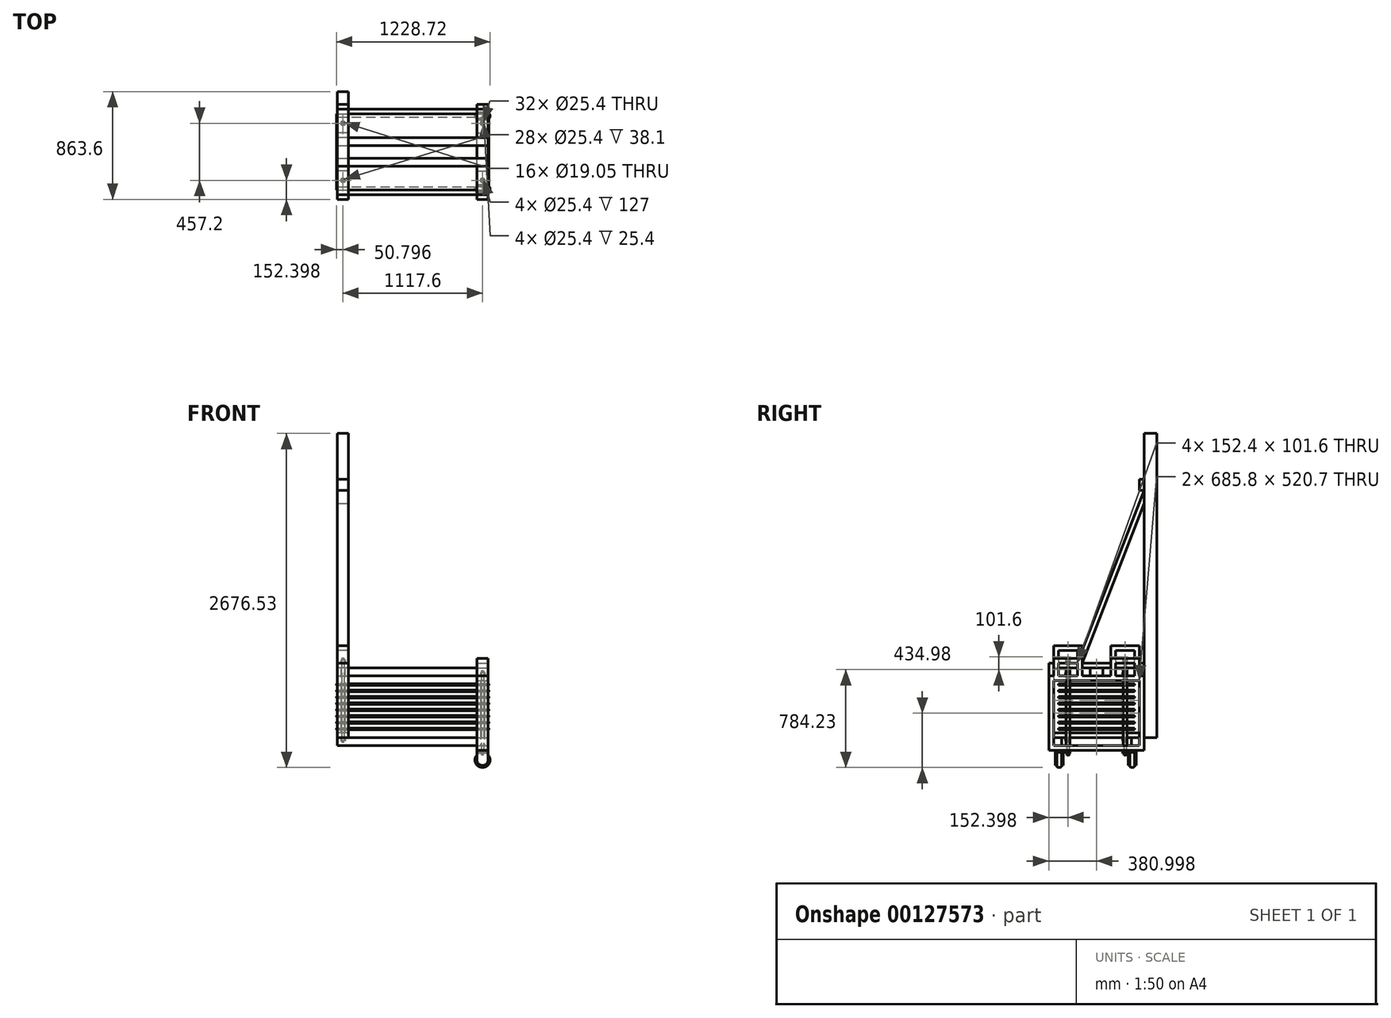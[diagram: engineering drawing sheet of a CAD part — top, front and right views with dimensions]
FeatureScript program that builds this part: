
annotation { "Feature Type Name" : "Feature", "Feature Type Description" : "" }
export const myFeature = defineFeature(function(context is Context, id is Id, definition is map)
    precondition{}
    {
        {
            var Q0;
            Q0=qCreatedBy(makeId("Top.planeOp"),FACE);
            var sketch = newSketch(context, id + "F0", { "sketchPlane" : qUnion([Q0])});
            skLineSegment(sketch, "E0.bottom", {"start": v(-608.46, 317.3) * mm, "end": v(610.74, 317.3) * mm});
            skLineSegment(sketch, "E0.top", {"start": v(-608.46, -292.3) * mm, "end": v(610.74, -292.3) * mm});
            skLineSegment(sketch, "E0.left", {"start": v(-608.46, 317.3) * mm, "end": v(-608.46, -292.3) * mm});
            skLineSegment(sketch, "E0.right", {"start": v(610.74, 317.3) * mm, "end": v(610.74, -292.3) * mm});
            skLineSegment(sketch, "E1", {"start": v(-608.46, 12.5) * mm, "end": v(-557.66, 12.5) * mm, "construction": true});
            skLineSegment(sketch, "E2", {"start": v(-557.66, 12.5) * mm, "end": v(559.94, 12.5) * mm, "construction": true});
            skPoint(sketch, "E2.endSnap0", {"position": v(610.74, 12.5) * mm});
            skLineSegment(sketch, "E3", {"start": v(559.94, 12.5) * mm, "end": v(610.74, 12.5) * mm, "construction": true});
            skLineSegment(sketch, "E4", {"start": v(-557.66, 12.5) * mm, "end": v(-557.66, 241.1) * mm, "construction": true});
            skLineSegment(sketch, "E5", {"start": v(-557.66, 241.1) * mm, "end": v(-557.66, 317.3) * mm, "construction": true});
            skLineSegment(sketch, "E6", {"start": v(-557.66, 12.5) * mm, "end": v(-557.66, -216.1) * mm, "construction": true});
            skLineSegment(sketch, "E7", {"start": v(-557.66, -216.1) * mm, "end": v(-557.66, -292.3) * mm, "construction": true});
            skLineSegment(sketch, "E8", {"start": v(559.94, 12.5) * mm, "end": v(559.94, 241.1) * mm, "construction": true});
            skLineSegment(sketch, "E9", {"start": v(559.94, 241.1) * mm, "end": v(559.94, 317.3) * mm, "construction": true});
            skLineSegment(sketch, "E10", {"start": v(559.94, 12.5) * mm, "end": v(559.94, -216.1) * mm, "construction": true});
            skLineSegment(sketch, "E11", {"start": v(559.94, -216.1) * mm, "end": v(559.94, -292.3) * mm, "construction": true});
            skCircle(sketch, "E12", {"center": v(-557.66, 241.1) * mm, "radius": 12.7 * mm});
            skCircle(sketch, "E13", {"center": v(-557.66, -216.1) * mm, "radius": 12.7 * mm});
            skCircle(sketch, "E14", {"center": v(559.94, 241.1) * mm, "radius": 12.7 * mm});
            skCircle(sketch, "E15", {"center": v(559.94, -216.1) * mm, "radius": 12.7 * mm});
            skSolve(sketch);
        }
        {
            var Q0;
            Q0 = qSketchRegion(id + "F0", true);
            extrude(context, id + "F1", {"entities" : qUnion([Q0]), "depth" : 12.7 * mm});
        }
        {
            var Q0;
            Q0=makeQuery(id+"F1.opExtrude","SWEPT_BODY",BODY,{"disambiguationData":[OSD([sQuery(id+"F0.wireOp",EDGE,"E0.bottom"),sQuery(id+"F0.wireOp",EDGE,"E0.top"),sQuery(id+"F0.wireOp",EDGE,"E0.left"),sQuery(id+"F0.wireOp",EDGE,"E0.right"),sQuery(id+"F0.wireOp",EDGE,"E12"),sQuery(id+"F0.wireOp",EDGE,"E13"),sQuery(id+"F0.wireOp",EDGE,"E14"),sQuery(id+"F0.wireOp",EDGE,"E15")])]});
            transform(context, id + "F2", {"entities" : qUnion([Q0]), "transformType" : TransformType.TRANSLATION_3D, "dx" : 0 * mm, "dy" : 0 * mm, "dz" : -50.8 * mm, "makeCopy" : true});
        }
        {
            var Q0;
            Q0=makeQuery(id+"F2.opPattern","COPY",BODY,{"derivedFrom":makeQuery(id+"F1.opExtrude","SWEPT_BODY",BODY,{"disambiguationData":[OSD([sQuery(id+"F0.wireOp",EDGE,"E0.bottom"),sQuery(id+"F0.wireOp",EDGE,"E0.top"),sQuery(id+"F0.wireOp",EDGE,"E0.left"),sQuery(id+"F0.wireOp",EDGE,"E0.right"),sQuery(id+"F0.wireOp",EDGE,"E12"),sQuery(id+"F0.wireOp",EDGE,"E13"),sQuery(id+"F0.wireOp",EDGE,"E14"),sQuery(id+"F0.wireOp",EDGE,"E15")])]}),"instanceName":"1"});
            transform(context, id + "F3", {"entities" : qUnion([Q0]), "transformType" : TransformType.TRANSLATION_3D, "dx" : 0 * mm, "dy" : 0 * mm, "dz" : -50.8 * mm, "makeCopy" : true});
        }
        {
            var Q0;
            Q0=makeQuery(id+"F3.opPattern","COPY",BODY,{"derivedFrom":makeQuery(id+"F2.opPattern","COPY",BODY,{"derivedFrom":makeQuery(id+"F1.opExtrude","SWEPT_BODY",BODY,{"disambiguationData":[OSD([sQuery(id+"F0.wireOp",EDGE,"E0.bottom"),sQuery(id+"F0.wireOp",EDGE,"E0.top"),sQuery(id+"F0.wireOp",EDGE,"E0.left"),sQuery(id+"F0.wireOp",EDGE,"E0.right"),sQuery(id+"F0.wireOp",EDGE,"E12"),sQuery(id+"F0.wireOp",EDGE,"E13"),sQuery(id+"F0.wireOp",EDGE,"E14"),sQuery(id+"F0.wireOp",EDGE,"E15")])]}),"instanceName":"1"}),"instanceName":"1"});
            transform(context, id + "F4", {"entities" : qUnion([Q0]), "transformType" : TransformType.TRANSLATION_3D, "dx" : 0 * mm, "dy" : 0 * mm, "dz" : -50.8 * mm, "makeCopy" : true});
        }
        {
            var Q0;
            Q0=makeQuery(id+"F4.opPattern","COPY",BODY,{"derivedFrom":makeQuery(id+"F3.opPattern","COPY",BODY,{"derivedFrom":makeQuery(id+"F2.opPattern","COPY",BODY,{"derivedFrom":makeQuery(id+"F1.opExtrude","SWEPT_BODY",BODY,{"disambiguationData":[OSD([sQuery(id+"F0.wireOp",EDGE,"E0.bottom"),sQuery(id+"F0.wireOp",EDGE,"E0.top"),sQuery(id+"F0.wireOp",EDGE,"E0.left"),sQuery(id+"F0.wireOp",EDGE,"E0.right"),sQuery(id+"F0.wireOp",EDGE,"E12"),sQuery(id+"F0.wireOp",EDGE,"E13"),sQuery(id+"F0.wireOp",EDGE,"E14"),sQuery(id+"F0.wireOp",EDGE,"E15")])]}),"instanceName":"1"}),"instanceName":"1"}),"instanceName":"1"});
            transform(context, id + "F5", {"entities" : qUnion([Q0]), "transformType" : TransformType.TRANSLATION_3D, "dx" : 0 * mm, "dy" : 0 * mm, "dz" : -50.8 * mm, "makeCopy" : true});
        }
        {
            var Q0;
            Q0=makeQuery(id+"F5.opPattern","COPY",BODY,{"derivedFrom":makeQuery(id+"F4.opPattern","COPY",BODY,{"derivedFrom":makeQuery(id+"F3.opPattern","COPY",BODY,{"derivedFrom":makeQuery(id+"F2.opPattern","COPY",BODY,{"derivedFrom":makeQuery(id+"F1.opExtrude","SWEPT_BODY",BODY,{"disambiguationData":[OSD([sQuery(id+"F0.wireOp",EDGE,"E0.bottom"),sQuery(id+"F0.wireOp",EDGE,"E0.top"),sQuery(id+"F0.wireOp",EDGE,"E0.left"),sQuery(id+"F0.wireOp",EDGE,"E0.right"),sQuery(id+"F0.wireOp",EDGE,"E12"),sQuery(id+"F0.wireOp",EDGE,"E13"),sQuery(id+"F0.wireOp",EDGE,"E14"),sQuery(id+"F0.wireOp",EDGE,"E15")])]}),"instanceName":"1"}),"instanceName":"1"}),"instanceName":"1"}),"instanceName":"1"});
            transform(context, id + "F6", {"entities" : qUnion([Q0]), "transformType" : TransformType.TRANSLATION_3D, "dx" : 0 * mm, "dy" : 0 * mm, "dz" : -50.8 * mm, "makeCopy" : true});
        }
        {
            var Q0;
            Q0=makeQuery(id+"F6.opPattern","COPY",BODY,{"derivedFrom":makeQuery(id+"F5.opPattern","COPY",BODY,{"derivedFrom":makeQuery(id+"F4.opPattern","COPY",BODY,{"derivedFrom":makeQuery(id+"F3.opPattern","COPY",BODY,{"derivedFrom":makeQuery(id+"F2.opPattern","COPY",BODY,{"derivedFrom":makeQuery(id+"F1.opExtrude","SWEPT_BODY",BODY,{"disambiguationData":[OSD([sQuery(id+"F0.wireOp",EDGE,"E0.bottom"),sQuery(id+"F0.wireOp",EDGE,"E0.top"),sQuery(id+"F0.wireOp",EDGE,"E0.left"),sQuery(id+"F0.wireOp",EDGE,"E0.right"),sQuery(id+"F0.wireOp",EDGE,"E12"),sQuery(id+"F0.wireOp",EDGE,"E13"),sQuery(id+"F0.wireOp",EDGE,"E14"),sQuery(id+"F0.wireOp",EDGE,"E15")])]}),"instanceName":"1"}),"instanceName":"1"}),"instanceName":"1"}),"instanceName":"1"}),"instanceName":"1"});
            transform(context, id + "F7", {"entities" : qUnion([Q0]), "transformType" : TransformType.TRANSLATION_3D, "dx" : 0 * mm, "dy" : 0 * mm, "dz" : -50.8 * mm, "makeCopy" : true});
        }
        {
            var Q0;
            Q0=makeQuery(id+"F7.opPattern","COPY",BODY,{"derivedFrom":makeQuery(id+"F6.opPattern","COPY",BODY,{"derivedFrom":makeQuery(id+"F5.opPattern","COPY",BODY,{"derivedFrom":makeQuery(id+"F4.opPattern","COPY",BODY,{"derivedFrom":makeQuery(id+"F3.opPattern","COPY",BODY,{"derivedFrom":makeQuery(id+"F2.opPattern","COPY",BODY,{"derivedFrom":makeQuery(id+"F1.opExtrude","SWEPT_BODY",BODY,{"disambiguationData":[OSD([sQuery(id+"F0.wireOp",EDGE,"E0.bottom"),sQuery(id+"F0.wireOp",EDGE,"E0.top"),sQuery(id+"F0.wireOp",EDGE,"E0.left"),sQuery(id+"F0.wireOp",EDGE,"E0.right"),sQuery(id+"F0.wireOp",EDGE,"E12"),sQuery(id+"F0.wireOp",EDGE,"E13"),sQuery(id+"F0.wireOp",EDGE,"E14"),sQuery(id+"F0.wireOp",EDGE,"E15")])]}),"instanceName":"1"}),"instanceName":"1"}),"instanceName":"1"}),"instanceName":"1"}),"instanceName":"1"}),"instanceName":"1"});
            transform(context, id + "F8", {"entities" : qUnion([Q0]), "transformType" : TransformType.TRANSLATION_3D, "dx" : 0 * mm, "dy" : 0 * mm, "dz" : -50.8 * mm, "makeCopy" : true});
        }
        {
            var Q0;
            Q0=makeQuery(id+"F1.opExtrude","CAP_FACE",FACE,{"disambiguationData":[OSD([sQuery(id+"F0.wireOp",EDGE,"E0.bottom"),sQuery(id+"F0.wireOp",EDGE,"E0.top"),sQuery(id+"F0.wireOp",EDGE,"E0.left"),sQuery(id+"F0.wireOp",EDGE,"E0.right"),sQuery(id+"F0.wireOp",EDGE,"E12"),sQuery(id+"F0.wireOp",EDGE,"E13"),sQuery(id+"F0.wireOp",EDGE,"E14"),sQuery(id+"F0.wireOp",EDGE,"E15")])],"isStart":false});
            var sketch = newSketch(context, id + "F9", { "sketchPlane" : qUnion([Q0])});
            skCircle(sketch, "E16", {"center": v(-557.66, 241.1) * mm, "radius": 15.88 * mm});
            skCircle(sketch, "E17", {"center": v(-557.66, -216.1) * mm, "radius": 15.88 * mm});
            skCircle(sketch, "E18", {"center": v(559.94, 241.1) * mm, "radius": 15.88 * mm});
            skCircle(sketch, "E19", {"center": v(559.94, -216.1) * mm, "radius": 15.88 * mm});
            skCircle(sketch, "E20", {"center": v(-557.66, 241.1) * mm, "radius": 12.7 * mm});
            skCircle(sketch, "E21", {"center": v(-557.66, -216.1) * mm, "radius": 12.7 * mm});
            skCircle(sketch, "E22", {"center": v(559.94, 241.1) * mm, "radius": 12.7 * mm});
            skCircle(sketch, "E23", {"center": v(559.94, -216.1) * mm, "radius": 12.7 * mm});
            skCircle(sketch, "E24", {"center": v(-557.66, 241.1) * mm, "radius": 9.53 * mm});
            skCircle(sketch, "E25", {"center": v(-557.66, -216.1) * mm, "radius": 9.53 * mm});
            skCircle(sketch, "E26", {"center": v(559.94, 241.1) * mm, "radius": 9.53 * mm});
            skCircle(sketch, "E27", {"center": v(559.94, -216.1) * mm, "radius": 9.53 * mm});
            skSolve(sketch);
        }
        {
            var Q0;
            Q0=makeQuery(id+"F9.imprint","IMPRINT",FACE,{"disambiguationData":[TD([[makeQuery(id+"F9.imprint","IMPRINT",EDGE,{"derivedFrom":sQuery(id+"F9.wireOp",EDGE,"E16")}),1.0]])]});
            var Q1;
            Q1=makeQuery(id+"F9.imprint","IMPRINT",FACE,{"disambiguationData":[TD([[makeQuery(id+"F9.imprint","IMPRINT",EDGE,{"derivedFrom":sQuery(id+"F9.wireOp",EDGE,"E17")}),1.0]])]});
            extrude(context, id + "F10", {"entities" : qUnion([Q0, Q1]), "depth" : 127 * mm, "hasSecondDirection" : true, "secondDirectionOppositeDirection" : true, "secondDirectionDepth" : 393.7 * mm});
        }
        {
            var Q0;
            Q0=makeQuery(id+"F1.opExtrude","SWEPT_BODY",BODY,{"disambiguationData":[OSD([sQuery(id+"F0.wireOp",EDGE,"E0.bottom"),sQuery(id+"F0.wireOp",EDGE,"E0.top"),sQuery(id+"F0.wireOp",EDGE,"E0.left"),sQuery(id+"F0.wireOp",EDGE,"E0.right"),sQuery(id+"F0.wireOp",EDGE,"E12"),sQuery(id+"F0.wireOp",EDGE,"E13"),sQuery(id+"F0.wireOp",EDGE,"E14"),sQuery(id+"F0.wireOp",EDGE,"E15")])]});
            transform(context, id + "F11", {"entities" : qUnion([Q0]), "transformType" : TransformType.TRANSLATION_3D, "dx" : 0 * mm, "dy" : 0 * mm, "dz" : 0 * mm, "makeCopy" : true});
        }
        {
            var Q0;
            Q0=makeQuery(id+"F1.opExtrude","SWEPT_BODY",BODY,{"disambiguationData":[OSD([sQuery(id+"F0.wireOp",EDGE,"E0.bottom"),sQuery(id+"F0.wireOp",EDGE,"E0.top"),sQuery(id+"F0.wireOp",EDGE,"E0.left"),sQuery(id+"F0.wireOp",EDGE,"E0.right"),sQuery(id+"F0.wireOp",EDGE,"E12"),sQuery(id+"F0.wireOp",EDGE,"E13"),sQuery(id+"F0.wireOp",EDGE,"E14"),sQuery(id+"F0.wireOp",EDGE,"E15")])]});
            var Q1;
            Q1=makeQuery(id+"F10.opExtrude","SWEPT_BODY",BODY,{"disambiguationData":[OSD([sQuery(id+"F9.wireOp",EDGE,"E16"),sQuery(id+"F9.wireOp",EDGE,"E20")])]});
            var Q2;
            Q2=makeQuery(id+"F10.opExtrude","SWEPT_BODY",BODY,{"disambiguationData":[OSD([sQuery(id+"F9.wireOp",EDGE,"E17"),sQuery(id+"F9.wireOp",EDGE,"E21")])]});
            booleanBodies(context, id + "F12", {"operationType" : BooleanOperationType.SUBTRACTION, "tools" : qUnion([Q0]), "targets" : qUnion([Q1, Q2])});
        }
        {
            var Q0;
            Q0=makeQuery(id+"F2.opPattern","COPY",BODY,{"derivedFrom":makeQuery(id+"F1.opExtrude","SWEPT_BODY",BODY,{"disambiguationData":[OSD([sQuery(id+"F0.wireOp",EDGE,"E0.bottom"),sQuery(id+"F0.wireOp",EDGE,"E0.top"),sQuery(id+"F0.wireOp",EDGE,"E0.left"),sQuery(id+"F0.wireOp",EDGE,"E0.right"),sQuery(id+"F0.wireOp",EDGE,"E12"),sQuery(id+"F0.wireOp",EDGE,"E13"),sQuery(id+"F0.wireOp",EDGE,"E14"),sQuery(id+"F0.wireOp",EDGE,"E15")])]}),"instanceName":"1"});
            transform(context, id + "F13", {"entities" : qUnion([Q0]), "transformType" : TransformType.TRANSLATION_3D, "dx" : 0 * mm, "dy" : 0 * mm, "dz" : 0 * mm, "makeCopy" : true});
        }
        {
            var Q0;
            Q0=makeQuery(id+"F2.opPattern","COPY",BODY,{"derivedFrom":makeQuery(id+"F1.opExtrude","SWEPT_BODY",BODY,{"disambiguationData":[OSD([sQuery(id+"F0.wireOp",EDGE,"E0.bottom"),sQuery(id+"F0.wireOp",EDGE,"E0.top"),sQuery(id+"F0.wireOp",EDGE,"E0.left"),sQuery(id+"F0.wireOp",EDGE,"E0.right"),sQuery(id+"F0.wireOp",EDGE,"E12"),sQuery(id+"F0.wireOp",EDGE,"E13"),sQuery(id+"F0.wireOp",EDGE,"E14"),sQuery(id+"F0.wireOp",EDGE,"E15")])]}),"instanceName":"1"});
            var Q1;
            Q1=makeQuery(id+"F12.opBoolean","SPLIT",BODY,{"disambiguationData":[OD(1.0)],"derivedFrom":makeQuery(id+"F10.opExtrude","SWEPT_BODY",BODY,{"disambiguationData":[OSD([sQuery(id+"F9.wireOp",EDGE,"E17"),sQuery(id+"F9.wireOp",EDGE,"E21")])]})});
            var Q2;
            Q2=makeQuery(id+"F12.opBoolean","SPLIT",BODY,{"disambiguationData":[OD(1.0)],"derivedFrom":makeQuery(id+"F10.opExtrude","SWEPT_BODY",BODY,{"disambiguationData":[OSD([sQuery(id+"F9.wireOp",EDGE,"E16"),sQuery(id+"F9.wireOp",EDGE,"E20")])]})});
            booleanBodies(context, id + "F14", {"operationType" : BooleanOperationType.SUBTRACTION, "tools" : qUnion([Q0]), "targets" : qUnion([Q1, Q2])});
        }
        {
            var Q0;
            Q0=makeQuery(id+"F13.opPattern","COPY",BODY,{"derivedFrom":makeQuery(id+"F2.opPattern","COPY",BODY,{"derivedFrom":makeQuery(id+"F1.opExtrude","SWEPT_BODY",BODY,{"disambiguationData":[OSD([sQuery(id+"F0.wireOp",EDGE,"E0.bottom"),sQuery(id+"F0.wireOp",EDGE,"E0.top"),sQuery(id+"F0.wireOp",EDGE,"E0.left"),sQuery(id+"F0.wireOp",EDGE,"E0.right"),sQuery(id+"F0.wireOp",EDGE,"E12"),sQuery(id+"F0.wireOp",EDGE,"E13"),sQuery(id+"F0.wireOp",EDGE,"E14"),sQuery(id+"F0.wireOp",EDGE,"E15")])]}),"instanceName":"1"}),"instanceName":"1"});
            transform(context, id + "F15", {"entities" : qUnion([Q0]), "transformType" : TransformType.TRANSLATION_3D, "dx" : 0 * mm, "dy" : 0 * mm, "dz" : 0 * mm, "makeCopy" : true});
        }
        {
            var Q0;
            Q0=makeQuery(id+"F13.opPattern","COPY",BODY,{"derivedFrom":makeQuery(id+"F2.opPattern","COPY",BODY,{"derivedFrom":makeQuery(id+"F1.opExtrude","SWEPT_BODY",BODY,{"disambiguationData":[OSD([sQuery(id+"F0.wireOp",EDGE,"E0.bottom"),sQuery(id+"F0.wireOp",EDGE,"E0.top"),sQuery(id+"F0.wireOp",EDGE,"E0.left"),sQuery(id+"F0.wireOp",EDGE,"E0.right"),sQuery(id+"F0.wireOp",EDGE,"E12"),sQuery(id+"F0.wireOp",EDGE,"E13"),sQuery(id+"F0.wireOp",EDGE,"E14"),sQuery(id+"F0.wireOp",EDGE,"E15")])]}),"instanceName":"1"}),"instanceName":"1"});
            var Q1;
            Q1=makeQuery(id+"F12.opBoolean","SPLIT",BODY,{"disambiguationData":[OD(0.0)],"derivedFrom":makeQuery(id+"F10.opExtrude","SWEPT_BODY",BODY,{"disambiguationData":[OSD([sQuery(id+"F9.wireOp",EDGE,"E16"),sQuery(id+"F9.wireOp",EDGE,"E20")])]})});
            var Q2;
            Q2=makeQuery(id+"F12.opBoolean","SPLIT",BODY,{"disambiguationData":[OD(0.0)],"derivedFrom":makeQuery(id+"F10.opExtrude","SWEPT_BODY",BODY,{"disambiguationData":[OSD([sQuery(id+"F9.wireOp",EDGE,"E17"),sQuery(id+"F9.wireOp",EDGE,"E21")])]})});
            booleanBodies(context, id + "F16", {"operationType" : BooleanOperationType.SUBTRACTION, "tools" : qUnion([Q0]), "targets" : qUnion([Q1, Q2])});
        }
        {
            var Q0;
            Q0=makeQuery(id+"F3.opPattern","COPY",BODY,{"derivedFrom":makeQuery(id+"F2.opPattern","COPY",BODY,{"derivedFrom":makeQuery(id+"F1.opExtrude","SWEPT_BODY",BODY,{"disambiguationData":[OSD([sQuery(id+"F0.wireOp",EDGE,"E0.bottom"),sQuery(id+"F0.wireOp",EDGE,"E0.top"),sQuery(id+"F0.wireOp",EDGE,"E0.left"),sQuery(id+"F0.wireOp",EDGE,"E0.right"),sQuery(id+"F0.wireOp",EDGE,"E12"),sQuery(id+"F0.wireOp",EDGE,"E13"),sQuery(id+"F0.wireOp",EDGE,"E14"),sQuery(id+"F0.wireOp",EDGE,"E15")])]}),"instanceName":"1"}),"instanceName":"1"});
            transform(context, id + "F17", {"entities" : qUnion([Q0]), "transformType" : TransformType.TRANSLATION_3D, "dx" : 0 * mm, "dy" : 0 * mm, "dz" : 0 * mm, "makeCopy" : true});
        }
        {
            var Q0;
            Q0=makeQuery(id+"F17.opPattern","COPY",BODY,{"derivedFrom":makeQuery(id+"F3.opPattern","COPY",BODY,{"derivedFrom":makeQuery(id+"F2.opPattern","COPY",BODY,{"derivedFrom":makeQuery(id+"F1.opExtrude","SWEPT_BODY",BODY,{"disambiguationData":[OSD([sQuery(id+"F0.wireOp",EDGE,"E0.bottom"),sQuery(id+"F0.wireOp",EDGE,"E0.top"),sQuery(id+"F0.wireOp",EDGE,"E0.left"),sQuery(id+"F0.wireOp",EDGE,"E0.right"),sQuery(id+"F0.wireOp",EDGE,"E12"),sQuery(id+"F0.wireOp",EDGE,"E13"),sQuery(id+"F0.wireOp",EDGE,"E14"),sQuery(id+"F0.wireOp",EDGE,"E15")])]}),"instanceName":"1"}),"instanceName":"1"}),"instanceName":"1"});
            var Q1;
            Q1=makeQuery(id+"F16.opBoolean","SPLIT",BODY,{"disambiguationData":[OD(0.0)],"derivedFrom":makeQuery(id+"F12.opBoolean","SPLIT",BODY,{"disambiguationData":[OD(0.0)],"derivedFrom":makeQuery(id+"F10.opExtrude","SWEPT_BODY",BODY,{"disambiguationData":[OSD([sQuery(id+"F9.wireOp",EDGE,"E16"),sQuery(id+"F9.wireOp",EDGE,"E20")])]})})});
            var Q2;
            Q2=makeQuery(id+"F16.opBoolean","SPLIT",BODY,{"disambiguationData":[OD(0.0)],"derivedFrom":makeQuery(id+"F12.opBoolean","SPLIT",BODY,{"disambiguationData":[OD(0.0)],"derivedFrom":makeQuery(id+"F10.opExtrude","SWEPT_BODY",BODY,{"disambiguationData":[OSD([sQuery(id+"F9.wireOp",EDGE,"E17"),sQuery(id+"F9.wireOp",EDGE,"E21")])]})})});
            booleanBodies(context, id + "F18", {"operationType" : BooleanOperationType.SUBTRACTION, "tools" : qUnion([Q0]), "targets" : qUnion([Q1, Q2])});
        }
        {
            var Q0;
            Q0=makeQuery(id+"F4.opPattern","COPY",BODY,{"derivedFrom":makeQuery(id+"F3.opPattern","COPY",BODY,{"derivedFrom":makeQuery(id+"F2.opPattern","COPY",BODY,{"derivedFrom":makeQuery(id+"F1.opExtrude","SWEPT_BODY",BODY,{"disambiguationData":[OSD([sQuery(id+"F0.wireOp",EDGE,"E0.bottom"),sQuery(id+"F0.wireOp",EDGE,"E0.top"),sQuery(id+"F0.wireOp",EDGE,"E0.left"),sQuery(id+"F0.wireOp",EDGE,"E0.right"),sQuery(id+"F0.wireOp",EDGE,"E12"),sQuery(id+"F0.wireOp",EDGE,"E13"),sQuery(id+"F0.wireOp",EDGE,"E14"),sQuery(id+"F0.wireOp",EDGE,"E15")])]}),"instanceName":"1"}),"instanceName":"1"}),"instanceName":"1"});
            transform(context, id + "F19", {"entities" : qUnion([Q0]), "transformType" : TransformType.TRANSLATION_3D, "dx" : 0 * mm, "dy" : 0 * mm, "dz" : 0 * mm, "makeCopy" : true});
        }
        {
            var Q0;
            Q0=makeQuery(id+"F19.opPattern","COPY",BODY,{"derivedFrom":makeQuery(id+"F4.opPattern","COPY",BODY,{"derivedFrom":makeQuery(id+"F3.opPattern","COPY",BODY,{"derivedFrom":makeQuery(id+"F2.opPattern","COPY",BODY,{"derivedFrom":makeQuery(id+"F1.opExtrude","SWEPT_BODY",BODY,{"disambiguationData":[OSD([sQuery(id+"F0.wireOp",EDGE,"E0.bottom"),sQuery(id+"F0.wireOp",EDGE,"E0.top"),sQuery(id+"F0.wireOp",EDGE,"E0.left"),sQuery(id+"F0.wireOp",EDGE,"E0.right"),sQuery(id+"F0.wireOp",EDGE,"E12"),sQuery(id+"F0.wireOp",EDGE,"E13"),sQuery(id+"F0.wireOp",EDGE,"E14"),sQuery(id+"F0.wireOp",EDGE,"E15")])]}),"instanceName":"1"}),"instanceName":"1"}),"instanceName":"1"}),"instanceName":"1"});
            var Q1;
            Q1=makeQuery(id+"F18.opBoolean","SPLIT",BODY,{"disambiguationData":[OD(0.0)],"derivedFrom":makeQuery(id+"F16.opBoolean","SPLIT",BODY,{"disambiguationData":[OD(0.0)],"derivedFrom":makeQuery(id+"F12.opBoolean","SPLIT",BODY,{"disambiguationData":[OD(0.0)],"derivedFrom":makeQuery(id+"F10.opExtrude","SWEPT_BODY",BODY,{"disambiguationData":[OSD([sQuery(id+"F9.wireOp",EDGE,"E16"),sQuery(id+"F9.wireOp",EDGE,"E20")])]})})})});
            var Q2;
            Q2=makeQuery(id+"F18.opBoolean","SPLIT",BODY,{"disambiguationData":[OD(0.0)],"derivedFrom":makeQuery(id+"F16.opBoolean","SPLIT",BODY,{"disambiguationData":[OD(0.0)],"derivedFrom":makeQuery(id+"F12.opBoolean","SPLIT",BODY,{"disambiguationData":[OD(0.0)],"derivedFrom":makeQuery(id+"F10.opExtrude","SWEPT_BODY",BODY,{"disambiguationData":[OSD([sQuery(id+"F9.wireOp",EDGE,"E17"),sQuery(id+"F9.wireOp",EDGE,"E21")])]})})})});
            booleanBodies(context, id + "F20", {"operationType" : BooleanOperationType.SUBTRACTION, "tools" : qUnion([Q0]), "targets" : qUnion([Q1, Q2])});
        }
        {
            var Q0;
            Q0=makeQuery(id+"F5.opPattern","COPY",BODY,{"derivedFrom":makeQuery(id+"F4.opPattern","COPY",BODY,{"derivedFrom":makeQuery(id+"F3.opPattern","COPY",BODY,{"derivedFrom":makeQuery(id+"F2.opPattern","COPY",BODY,{"derivedFrom":makeQuery(id+"F1.opExtrude","SWEPT_BODY",BODY,{"disambiguationData":[OSD([sQuery(id+"F0.wireOp",EDGE,"E0.bottom"),sQuery(id+"F0.wireOp",EDGE,"E0.top"),sQuery(id+"F0.wireOp",EDGE,"E0.left"),sQuery(id+"F0.wireOp",EDGE,"E0.right"),sQuery(id+"F0.wireOp",EDGE,"E12"),sQuery(id+"F0.wireOp",EDGE,"E13"),sQuery(id+"F0.wireOp",EDGE,"E14"),sQuery(id+"F0.wireOp",EDGE,"E15")])]}),"instanceName":"1"}),"instanceName":"1"}),"instanceName":"1"}),"instanceName":"1"});
            transform(context, id + "F21", {"entities" : qUnion([Q0]), "transformType" : TransformType.TRANSLATION_3D, "dx" : 0 * mm, "dy" : 0 * mm, "dz" : 0 * mm, "makeCopy" : true});
        }
        {
            var Q0;
            Q0=makeQuery(id+"F21.opPattern","COPY",BODY,{"derivedFrom":makeQuery(id+"F5.opPattern","COPY",BODY,{"derivedFrom":makeQuery(id+"F4.opPattern","COPY",BODY,{"derivedFrom":makeQuery(id+"F3.opPattern","COPY",BODY,{"derivedFrom":makeQuery(id+"F2.opPattern","COPY",BODY,{"derivedFrom":makeQuery(id+"F1.opExtrude","SWEPT_BODY",BODY,{"disambiguationData":[OSD([sQuery(id+"F0.wireOp",EDGE,"E0.bottom"),sQuery(id+"F0.wireOp",EDGE,"E0.top"),sQuery(id+"F0.wireOp",EDGE,"E0.left"),sQuery(id+"F0.wireOp",EDGE,"E0.right"),sQuery(id+"F0.wireOp",EDGE,"E12"),sQuery(id+"F0.wireOp",EDGE,"E13"),sQuery(id+"F0.wireOp",EDGE,"E14"),sQuery(id+"F0.wireOp",EDGE,"E15")])]}),"instanceName":"1"}),"instanceName":"1"}),"instanceName":"1"}),"instanceName":"1"}),"instanceName":"1"});
            var Q1;
            Q1=makeQuery(id+"F20.opBoolean","SPLIT",BODY,{"disambiguationData":[OD(0.0)],"derivedFrom":makeQuery(id+"F18.opBoolean","SPLIT",BODY,{"disambiguationData":[OD(0.0)],"derivedFrom":makeQuery(id+"F16.opBoolean","SPLIT",BODY,{"disambiguationData":[OD(0.0)],"derivedFrom":makeQuery(id+"F12.opBoolean","SPLIT",BODY,{"disambiguationData":[OD(0.0)],"derivedFrom":makeQuery(id+"F10.opExtrude","SWEPT_BODY",BODY,{"disambiguationData":[OSD([sQuery(id+"F9.wireOp",EDGE,"E16"),sQuery(id+"F9.wireOp",EDGE,"E20")])]})})})})});
            var Q2;
            Q2=makeQuery(id+"F20.opBoolean","SPLIT",BODY,{"disambiguationData":[OD(0.0)],"derivedFrom":makeQuery(id+"F18.opBoolean","SPLIT",BODY,{"disambiguationData":[OD(0.0)],"derivedFrom":makeQuery(id+"F16.opBoolean","SPLIT",BODY,{"disambiguationData":[OD(0.0)],"derivedFrom":makeQuery(id+"F12.opBoolean","SPLIT",BODY,{"disambiguationData":[OD(0.0)],"derivedFrom":makeQuery(id+"F10.opExtrude","SWEPT_BODY",BODY,{"disambiguationData":[OSD([sQuery(id+"F9.wireOp",EDGE,"E17"),sQuery(id+"F9.wireOp",EDGE,"E21")])]})})})})});
            booleanBodies(context, id + "F22", {"operationType" : BooleanOperationType.SUBTRACTION, "tools" : qUnion([Q0]), "targets" : qUnion([Q1, Q2])});
        }
        {
            var Q0;
            Q0=makeQuery(id+"F6.opPattern","COPY",BODY,{"derivedFrom":makeQuery(id+"F5.opPattern","COPY",BODY,{"derivedFrom":makeQuery(id+"F4.opPattern","COPY",BODY,{"derivedFrom":makeQuery(id+"F3.opPattern","COPY",BODY,{"derivedFrom":makeQuery(id+"F2.opPattern","COPY",BODY,{"derivedFrom":makeQuery(id+"F1.opExtrude","SWEPT_BODY",BODY,{"disambiguationData":[OSD([sQuery(id+"F0.wireOp",EDGE,"E0.bottom"),sQuery(id+"F0.wireOp",EDGE,"E0.top"),sQuery(id+"F0.wireOp",EDGE,"E0.left"),sQuery(id+"F0.wireOp",EDGE,"E0.right"),sQuery(id+"F0.wireOp",EDGE,"E12"),sQuery(id+"F0.wireOp",EDGE,"E13"),sQuery(id+"F0.wireOp",EDGE,"E14"),sQuery(id+"F0.wireOp",EDGE,"E15")])]}),"instanceName":"1"}),"instanceName":"1"}),"instanceName":"1"}),"instanceName":"1"}),"instanceName":"1"});
            transform(context, id + "F23", {"entities" : qUnion([Q0]), "transformType" : TransformType.TRANSLATION_3D, "dx" : 0 * mm, "dy" : 0 * mm, "dz" : 0 * mm, "makeCopy" : true});
        }
        {
            var Q0;
            Q0=makeQuery(id+"F23.opPattern","COPY",BODY,{"derivedFrom":makeQuery(id+"F6.opPattern","COPY",BODY,{"derivedFrom":makeQuery(id+"F5.opPattern","COPY",BODY,{"derivedFrom":makeQuery(id+"F4.opPattern","COPY",BODY,{"derivedFrom":makeQuery(id+"F3.opPattern","COPY",BODY,{"derivedFrom":makeQuery(id+"F2.opPattern","COPY",BODY,{"derivedFrom":makeQuery(id+"F1.opExtrude","SWEPT_BODY",BODY,{"disambiguationData":[OSD([sQuery(id+"F0.wireOp",EDGE,"E0.bottom"),sQuery(id+"F0.wireOp",EDGE,"E0.top"),sQuery(id+"F0.wireOp",EDGE,"E0.left"),sQuery(id+"F0.wireOp",EDGE,"E0.right"),sQuery(id+"F0.wireOp",EDGE,"E12"),sQuery(id+"F0.wireOp",EDGE,"E13"),sQuery(id+"F0.wireOp",EDGE,"E14"),sQuery(id+"F0.wireOp",EDGE,"E15")])]}),"instanceName":"1"}),"instanceName":"1"}),"instanceName":"1"}),"instanceName":"1"}),"instanceName":"1"}),"instanceName":"1"});
            var Q1;
            Q1=makeQuery(id+"F22.opBoolean","SPLIT",BODY,{"disambiguationData":[OD(0.0)],"derivedFrom":makeQuery(id+"F20.opBoolean","SPLIT",BODY,{"disambiguationData":[OD(0.0)],"derivedFrom":makeQuery(id+"F18.opBoolean","SPLIT",BODY,{"disambiguationData":[OD(0.0)],"derivedFrom":makeQuery(id+"F16.opBoolean","SPLIT",BODY,{"disambiguationData":[OD(0.0)],"derivedFrom":makeQuery(id+"F12.opBoolean","SPLIT",BODY,{"disambiguationData":[OD(0.0)],"derivedFrom":makeQuery(id+"F10.opExtrude","SWEPT_BODY",BODY,{"disambiguationData":[OSD([sQuery(id+"F9.wireOp",EDGE,"E16"),sQuery(id+"F9.wireOp",EDGE,"E20")])]})})})})})});
            var Q2;
            Q2=makeQuery(id+"F22.opBoolean","SPLIT",BODY,{"disambiguationData":[OD(0.0)],"derivedFrom":makeQuery(id+"F20.opBoolean","SPLIT",BODY,{"disambiguationData":[OD(0.0)],"derivedFrom":makeQuery(id+"F18.opBoolean","SPLIT",BODY,{"disambiguationData":[OD(0.0)],"derivedFrom":makeQuery(id+"F16.opBoolean","SPLIT",BODY,{"disambiguationData":[OD(0.0)],"derivedFrom":makeQuery(id+"F12.opBoolean","SPLIT",BODY,{"disambiguationData":[OD(0.0)],"derivedFrom":makeQuery(id+"F10.opExtrude","SWEPT_BODY",BODY,{"disambiguationData":[OSD([sQuery(id+"F9.wireOp",EDGE,"E17"),sQuery(id+"F9.wireOp",EDGE,"E21")])]})})})})})});
            booleanBodies(context, id + "F24", {"operationType" : BooleanOperationType.SUBTRACTION, "tools" : qUnion([Q0]), "targets" : qUnion([Q1, Q2])});
        }
        {
            var Q0;
            Q0=makeQuery(id+"F7.opPattern","COPY",BODY,{"derivedFrom":makeQuery(id+"F6.opPattern","COPY",BODY,{"derivedFrom":makeQuery(id+"F5.opPattern","COPY",BODY,{"derivedFrom":makeQuery(id+"F4.opPattern","COPY",BODY,{"derivedFrom":makeQuery(id+"F3.opPattern","COPY",BODY,{"derivedFrom":makeQuery(id+"F2.opPattern","COPY",BODY,{"derivedFrom":makeQuery(id+"F1.opExtrude","SWEPT_BODY",BODY,{"disambiguationData":[OSD([sQuery(id+"F0.wireOp",EDGE,"E0.bottom"),sQuery(id+"F0.wireOp",EDGE,"E0.top"),sQuery(id+"F0.wireOp",EDGE,"E0.left"),sQuery(id+"F0.wireOp",EDGE,"E0.right"),sQuery(id+"F0.wireOp",EDGE,"E12"),sQuery(id+"F0.wireOp",EDGE,"E13"),sQuery(id+"F0.wireOp",EDGE,"E14"),sQuery(id+"F0.wireOp",EDGE,"E15")])]}),"instanceName":"1"}),"instanceName":"1"}),"instanceName":"1"}),"instanceName":"1"}),"instanceName":"1"}),"instanceName":"1"});
            transform(context, id + "F25", {"entities" : qUnion([Q0]), "transformType" : TransformType.TRANSLATION_3D, "dx" : 0 * mm, "dy" : 0 * mm, "dz" : 0 * mm, "makeCopy" : true});
        }
        {
            var Q0;
            Q0=makeQuery(id+"F25.opPattern","COPY",BODY,{"derivedFrom":makeQuery(id+"F7.opPattern","COPY",BODY,{"derivedFrom":makeQuery(id+"F6.opPattern","COPY",BODY,{"derivedFrom":makeQuery(id+"F5.opPattern","COPY",BODY,{"derivedFrom":makeQuery(id+"F4.opPattern","COPY",BODY,{"derivedFrom":makeQuery(id+"F3.opPattern","COPY",BODY,{"derivedFrom":makeQuery(id+"F2.opPattern","COPY",BODY,{"derivedFrom":makeQuery(id+"F1.opExtrude","SWEPT_BODY",BODY,{"disambiguationData":[OSD([sQuery(id+"F0.wireOp",EDGE,"E0.bottom"),sQuery(id+"F0.wireOp",EDGE,"E0.top"),sQuery(id+"F0.wireOp",EDGE,"E0.left"),sQuery(id+"F0.wireOp",EDGE,"E0.right"),sQuery(id+"F0.wireOp",EDGE,"E12"),sQuery(id+"F0.wireOp",EDGE,"E13"),sQuery(id+"F0.wireOp",EDGE,"E14"),sQuery(id+"F0.wireOp",EDGE,"E15")])]}),"instanceName":"1"}),"instanceName":"1"}),"instanceName":"1"}),"instanceName":"1"}),"instanceName":"1"}),"instanceName":"1"}),"instanceName":"1"});
            var Q1;
            Q1=makeQuery(id+"F24.opBoolean","SPLIT",BODY,{"disambiguationData":[OD(0.0)],"derivedFrom":makeQuery(id+"F22.opBoolean","SPLIT",BODY,{"disambiguationData":[OD(0.0)],"derivedFrom":makeQuery(id+"F20.opBoolean","SPLIT",BODY,{"disambiguationData":[OD(0.0)],"derivedFrom":makeQuery(id+"F18.opBoolean","SPLIT",BODY,{"disambiguationData":[OD(0.0)],"derivedFrom":makeQuery(id+"F16.opBoolean","SPLIT",BODY,{"disambiguationData":[OD(0.0)],"derivedFrom":makeQuery(id+"F12.opBoolean","SPLIT",BODY,{"disambiguationData":[OD(0.0)],"derivedFrom":makeQuery(id+"F10.opExtrude","SWEPT_BODY",BODY,{"disambiguationData":[OSD([sQuery(id+"F9.wireOp",EDGE,"E16"),sQuery(id+"F9.wireOp",EDGE,"E20")])]})})})})})})});
            var Q2;
            Q2=makeQuery(id+"F24.opBoolean","SPLIT",BODY,{"disambiguationData":[OD(0.0)],"derivedFrom":makeQuery(id+"F22.opBoolean","SPLIT",BODY,{"disambiguationData":[OD(0.0)],"derivedFrom":makeQuery(id+"F20.opBoolean","SPLIT",BODY,{"disambiguationData":[OD(0.0)],"derivedFrom":makeQuery(id+"F18.opBoolean","SPLIT",BODY,{"disambiguationData":[OD(0.0)],"derivedFrom":makeQuery(id+"F16.opBoolean","SPLIT",BODY,{"disambiguationData":[OD(0.0)],"derivedFrom":makeQuery(id+"F12.opBoolean","SPLIT",BODY,{"disambiguationData":[OD(0.0)],"derivedFrom":makeQuery(id+"F10.opExtrude","SWEPT_BODY",BODY,{"disambiguationData":[OSD([sQuery(id+"F9.wireOp",EDGE,"E17"),sQuery(id+"F9.wireOp",EDGE,"E21")])]})})})})})})});
            booleanBodies(context, id + "F26", {"operationType" : BooleanOperationType.SUBTRACTION, "tools" : qUnion([Q0]), "targets" : qUnion([Q1, Q2])});
        }
        {
            var Q0;
            Q0=makeQuery(id+"F8.opPattern","COPY",BODY,{"derivedFrom":makeQuery(id+"F7.opPattern","COPY",BODY,{"derivedFrom":makeQuery(id+"F6.opPattern","COPY",BODY,{"derivedFrom":makeQuery(id+"F5.opPattern","COPY",BODY,{"derivedFrom":makeQuery(id+"F4.opPattern","COPY",BODY,{"derivedFrom":makeQuery(id+"F3.opPattern","COPY",BODY,{"derivedFrom":makeQuery(id+"F2.opPattern","COPY",BODY,{"derivedFrom":makeQuery(id+"F1.opExtrude","SWEPT_BODY",BODY,{"disambiguationData":[OSD([sQuery(id+"F0.wireOp",EDGE,"E0.bottom"),sQuery(id+"F0.wireOp",EDGE,"E0.top"),sQuery(id+"F0.wireOp",EDGE,"E0.left"),sQuery(id+"F0.wireOp",EDGE,"E0.right"),sQuery(id+"F0.wireOp",EDGE,"E12"),sQuery(id+"F0.wireOp",EDGE,"E13"),sQuery(id+"F0.wireOp",EDGE,"E14"),sQuery(id+"F0.wireOp",EDGE,"E15")])]}),"instanceName":"1"}),"instanceName":"1"}),"instanceName":"1"}),"instanceName":"1"}),"instanceName":"1"}),"instanceName":"1"}),"instanceName":"1"});
            transform(context, id + "F27", {"entities" : qUnion([Q0]), "transformType" : TransformType.TRANSLATION_3D, "dx" : 0 * mm, "dy" : 0 * mm, "dz" : 0 * mm, "makeCopy" : true});
        }
        {
            var Q0;
            Q0=makeQuery(id+"F27.opPattern","COPY",BODY,{"derivedFrom":makeQuery(id+"F8.opPattern","COPY",BODY,{"derivedFrom":makeQuery(id+"F7.opPattern","COPY",BODY,{"derivedFrom":makeQuery(id+"F6.opPattern","COPY",BODY,{"derivedFrom":makeQuery(id+"F5.opPattern","COPY",BODY,{"derivedFrom":makeQuery(id+"F4.opPattern","COPY",BODY,{"derivedFrom":makeQuery(id+"F3.opPattern","COPY",BODY,{"derivedFrom":makeQuery(id+"F2.opPattern","COPY",BODY,{"derivedFrom":makeQuery(id+"F1.opExtrude","SWEPT_BODY",BODY,{"disambiguationData":[OSD([sQuery(id+"F0.wireOp",EDGE,"E0.bottom"),sQuery(id+"F0.wireOp",EDGE,"E0.top"),sQuery(id+"F0.wireOp",EDGE,"E0.left"),sQuery(id+"F0.wireOp",EDGE,"E0.right"),sQuery(id+"F0.wireOp",EDGE,"E12"),sQuery(id+"F0.wireOp",EDGE,"E13"),sQuery(id+"F0.wireOp",EDGE,"E14"),sQuery(id+"F0.wireOp",EDGE,"E15")])]}),"instanceName":"1"}),"instanceName":"1"}),"instanceName":"1"}),"instanceName":"1"}),"instanceName":"1"}),"instanceName":"1"}),"instanceName":"1"}),"instanceName":"1"});
            var Q1;
            Q1=makeQuery(id+"F26.opBoolean","SPLIT",BODY,{"disambiguationData":[OD(0.0)],"derivedFrom":makeQuery(id+"F24.opBoolean","SPLIT",BODY,{"disambiguationData":[OD(0.0)],"derivedFrom":makeQuery(id+"F22.opBoolean","SPLIT",BODY,{"disambiguationData":[OD(0.0)],"derivedFrom":makeQuery(id+"F20.opBoolean","SPLIT",BODY,{"disambiguationData":[OD(0.0)],"derivedFrom":makeQuery(id+"F18.opBoolean","SPLIT",BODY,{"disambiguationData":[OD(0.0)],"derivedFrom":makeQuery(id+"F16.opBoolean","SPLIT",BODY,{"disambiguationData":[OD(0.0)],"derivedFrom":makeQuery(id+"F12.opBoolean","SPLIT",BODY,{"disambiguationData":[OD(0.0)],"derivedFrom":makeQuery(id+"F10.opExtrude","SWEPT_BODY",BODY,{"disambiguationData":[OSD([sQuery(id+"F9.wireOp",EDGE,"E16"),sQuery(id+"F9.wireOp",EDGE,"E20")])]})})})})})})})});
            var Q2;
            Q2=makeQuery(id+"F26.opBoolean","SPLIT",BODY,{"disambiguationData":[OD(0.0)],"derivedFrom":makeQuery(id+"F24.opBoolean","SPLIT",BODY,{"disambiguationData":[OD(0.0)],"derivedFrom":makeQuery(id+"F22.opBoolean","SPLIT",BODY,{"disambiguationData":[OD(0.0)],"derivedFrom":makeQuery(id+"F20.opBoolean","SPLIT",BODY,{"disambiguationData":[OD(0.0)],"derivedFrom":makeQuery(id+"F18.opBoolean","SPLIT",BODY,{"disambiguationData":[OD(0.0)],"derivedFrom":makeQuery(id+"F16.opBoolean","SPLIT",BODY,{"disambiguationData":[OD(0.0)],"derivedFrom":makeQuery(id+"F12.opBoolean","SPLIT",BODY,{"disambiguationData":[OD(0.0)],"derivedFrom":makeQuery(id+"F10.opExtrude","SWEPT_BODY",BODY,{"disambiguationData":[OSD([sQuery(id+"F9.wireOp",EDGE,"E17"),sQuery(id+"F9.wireOp",EDGE,"E21")])]})})})})})})})});
            booleanBodies(context, id + "F28", {"operationType" : BooleanOperationType.SUBTRACTION, "tools" : qUnion([Q0]), "targets" : qUnion([Q1, Q2])});
        }
        {
            var Q0;
            Q0=makeQuery(id+"F9.imprint","IMPRINT",FACE,{"disambiguationData":[TD([[makeQuery(id+"F9.imprint","IMPRINT",EDGE,{"derivedFrom":sQuery(id+"F9.wireOp",EDGE,"E18")}),1.0]])]});
            var Q1;
            Q1=makeQuery(id+"F9.imprint","IMPRINT",FACE,{"disambiguationData":[TD([[makeQuery(id+"F9.imprint","IMPRINT",EDGE,{"derivedFrom":sQuery(id+"F9.wireOp",EDGE,"E19")}),1.0]])]});
            extrude(context, id + "F29", {"entities" : qUnion([Q0, Q1]), "depth" : 25.4 * mm, "hasSecondDirection" : true, "secondDirectionOppositeDirection" : true, "secondDirectionDepth" : 495.3 * mm});
        }
        {
            var Q0;
            Q0=makeQuery(id+"F11.opPattern","COPY",BODY,{"derivedFrom":makeQuery(id+"F1.opExtrude","SWEPT_BODY",BODY,{"disambiguationData":[OSD([sQuery(id+"F0.wireOp",EDGE,"E0.bottom"),sQuery(id+"F0.wireOp",EDGE,"E0.top"),sQuery(id+"F0.wireOp",EDGE,"E0.left"),sQuery(id+"F0.wireOp",EDGE,"E0.right"),sQuery(id+"F0.wireOp",EDGE,"E12"),sQuery(id+"F0.wireOp",EDGE,"E13"),sQuery(id+"F0.wireOp",EDGE,"E14"),sQuery(id+"F0.wireOp",EDGE,"E15")])]}),"instanceName":"1"});
            transform(context, id + "F30", {"entities" : qUnion([Q0]), "transformType" : TransformType.TRANSLATION_3D, "dx" : 0 * mm, "dy" : 0 * mm, "dz" : 0 * mm, "makeCopy" : true});
        }
        {
            var Q0;
            Q0=makeQuery(id+"F11.opPattern","COPY",BODY,{"derivedFrom":makeQuery(id+"F1.opExtrude","SWEPT_BODY",BODY,{"disambiguationData":[OSD([sQuery(id+"F0.wireOp",EDGE,"E0.bottom"),sQuery(id+"F0.wireOp",EDGE,"E0.top"),sQuery(id+"F0.wireOp",EDGE,"E0.left"),sQuery(id+"F0.wireOp",EDGE,"E0.right"),sQuery(id+"F0.wireOp",EDGE,"E12"),sQuery(id+"F0.wireOp",EDGE,"E13"),sQuery(id+"F0.wireOp",EDGE,"E14"),sQuery(id+"F0.wireOp",EDGE,"E15")])]}),"instanceName":"1"});
            var Q1;
            Q1=makeQuery(id+"F29.opExtrude","SWEPT_BODY",BODY,{"disambiguationData":[OSD([sQuery(id+"F9.wireOp",EDGE,"E18"),sQuery(id+"F9.wireOp",EDGE,"E22")])]});
            var Q2;
            Q2=makeQuery(id+"F29.opExtrude","SWEPT_BODY",BODY,{"disambiguationData":[OSD([sQuery(id+"F9.wireOp",EDGE,"E19"),sQuery(id+"F9.wireOp",EDGE,"E23")])]});
            booleanBodies(context, id + "F31", {"operationType" : BooleanOperationType.SUBTRACTION, "tools" : qUnion([Q0]), "targets" : qUnion([Q1, Q2])});
        }
        {
            var Q0;
            Q0=makeQuery(id+"F15.opPattern","COPY",BODY,{"derivedFrom":makeQuery(id+"F13.opPattern","COPY",BODY,{"derivedFrom":makeQuery(id+"F2.opPattern","COPY",BODY,{"derivedFrom":makeQuery(id+"F1.opExtrude","SWEPT_BODY",BODY,{"disambiguationData":[OSD([sQuery(id+"F0.wireOp",EDGE,"E0.bottom"),sQuery(id+"F0.wireOp",EDGE,"E0.top"),sQuery(id+"F0.wireOp",EDGE,"E0.left"),sQuery(id+"F0.wireOp",EDGE,"E0.right"),sQuery(id+"F0.wireOp",EDGE,"E12"),sQuery(id+"F0.wireOp",EDGE,"E13"),sQuery(id+"F0.wireOp",EDGE,"E14"),sQuery(id+"F0.wireOp",EDGE,"E15")])]}),"instanceName":"1"}),"instanceName":"1"}),"instanceName":"1"});
            transform(context, id + "F32", {"entities" : qUnion([Q0]), "transformType" : TransformType.TRANSLATION_3D, "dx" : 0 * mm, "dy" : 0 * mm, "dz" : 0 * mm, "makeCopy" : true});
        }
        {
            var Q0;
            Q0=makeQuery(id+"F32.opPattern","COPY",BODY,{"derivedFrom":makeQuery(id+"F15.opPattern","COPY",BODY,{"derivedFrom":makeQuery(id+"F13.opPattern","COPY",BODY,{"derivedFrom":makeQuery(id+"F2.opPattern","COPY",BODY,{"derivedFrom":makeQuery(id+"F1.opExtrude","SWEPT_BODY",BODY,{"disambiguationData":[OSD([sQuery(id+"F0.wireOp",EDGE,"E0.bottom"),sQuery(id+"F0.wireOp",EDGE,"E0.top"),sQuery(id+"F0.wireOp",EDGE,"E0.left"),sQuery(id+"F0.wireOp",EDGE,"E0.right"),sQuery(id+"F0.wireOp",EDGE,"E12"),sQuery(id+"F0.wireOp",EDGE,"E13"),sQuery(id+"F0.wireOp",EDGE,"E14"),sQuery(id+"F0.wireOp",EDGE,"E15")])]}),"instanceName":"1"}),"instanceName":"1"}),"instanceName":"1"}),"instanceName":"1"});
            var Q1;
            Q1=makeQuery(id+"F31.opBoolean","SPLIT",BODY,{"disambiguationData":[OD(0.0)],"derivedFrom":makeQuery(id+"F29.opExtrude","SWEPT_BODY",BODY,{"disambiguationData":[OSD([sQuery(id+"F9.wireOp",EDGE,"E18"),sQuery(id+"F9.wireOp",EDGE,"E22")])]})});
            var Q2;
            Q2=makeQuery(id+"F31.opBoolean","SPLIT",BODY,{"disambiguationData":[OD(0.0)],"derivedFrom":makeQuery(id+"F29.opExtrude","SWEPT_BODY",BODY,{"disambiguationData":[OSD([sQuery(id+"F9.wireOp",EDGE,"E19"),sQuery(id+"F9.wireOp",EDGE,"E23")])]})});
            booleanBodies(context, id + "F33", {"operationType" : BooleanOperationType.SUBTRACTION, "tools" : qUnion([Q0]), "targets" : qUnion([Q1, Q2])});
        }
        {
            var Q0;
            Q0=makeQuery(id+"F3.opPattern","COPY",BODY,{"derivedFrom":makeQuery(id+"F2.opPattern","COPY",BODY,{"derivedFrom":makeQuery(id+"F1.opExtrude","SWEPT_BODY",BODY,{"disambiguationData":[OSD([sQuery(id+"F0.wireOp",EDGE,"E0.bottom"),sQuery(id+"F0.wireOp",EDGE,"E0.top"),sQuery(id+"F0.wireOp",EDGE,"E0.left"),sQuery(id+"F0.wireOp",EDGE,"E0.right"),sQuery(id+"F0.wireOp",EDGE,"E12"),sQuery(id+"F0.wireOp",EDGE,"E13"),sQuery(id+"F0.wireOp",EDGE,"E14"),sQuery(id+"F0.wireOp",EDGE,"E15")])]}),"instanceName":"1"}),"instanceName":"1"});
            transform(context, id + "F34", {"entities" : qUnion([Q0]), "transformType" : TransformType.TRANSLATION_3D, "dx" : 0 * mm, "dy" : 0 * mm, "dz" : 0 * mm, "makeCopy" : true});
        }
        {
            var Q0;
            Q0=makeQuery(id+"F3.opPattern","COPY",BODY,{"derivedFrom":makeQuery(id+"F2.opPattern","COPY",BODY,{"derivedFrom":makeQuery(id+"F1.opExtrude","SWEPT_BODY",BODY,{"disambiguationData":[OSD([sQuery(id+"F0.wireOp",EDGE,"E0.bottom"),sQuery(id+"F0.wireOp",EDGE,"E0.top"),sQuery(id+"F0.wireOp",EDGE,"E0.left"),sQuery(id+"F0.wireOp",EDGE,"E0.right"),sQuery(id+"F0.wireOp",EDGE,"E12"),sQuery(id+"F0.wireOp",EDGE,"E13"),sQuery(id+"F0.wireOp",EDGE,"E14"),sQuery(id+"F0.wireOp",EDGE,"E15")])]}),"instanceName":"1"}),"instanceName":"1"});
            var Q1;
            Q1=makeQuery(id+"F33.opBoolean","SPLIT",BODY,{"disambiguationData":[OD(0.0)],"derivedFrom":makeQuery(id+"F31.opBoolean","SPLIT",BODY,{"disambiguationData":[OD(0.0)],"derivedFrom":makeQuery(id+"F29.opExtrude","SWEPT_BODY",BODY,{"disambiguationData":[OSD([sQuery(id+"F9.wireOp",EDGE,"E18"),sQuery(id+"F9.wireOp",EDGE,"E22")])]})})});
            var Q2;
            Q2=makeQuery(id+"F33.opBoolean","SPLIT",BODY,{"disambiguationData":[OD(0.0)],"derivedFrom":makeQuery(id+"F31.opBoolean","SPLIT",BODY,{"disambiguationData":[OD(0.0)],"derivedFrom":makeQuery(id+"F29.opExtrude","SWEPT_BODY",BODY,{"disambiguationData":[OSD([sQuery(id+"F9.wireOp",EDGE,"E19"),sQuery(id+"F9.wireOp",EDGE,"E23")])]})})});
            booleanBodies(context, id + "F35", {"operationType" : BooleanOperationType.SUBTRACTION, "tools" : qUnion([Q0]), "targets" : qUnion([Q1, Q2])});
        }
        {
            var Q0;
            Q0=makeQuery(id+"F5.opPattern","COPY",BODY,{"derivedFrom":makeQuery(id+"F4.opPattern","COPY",BODY,{"derivedFrom":makeQuery(id+"F3.opPattern","COPY",BODY,{"derivedFrom":makeQuery(id+"F2.opPattern","COPY",BODY,{"derivedFrom":makeQuery(id+"F1.opExtrude","SWEPT_BODY",BODY,{"disambiguationData":[OSD([sQuery(id+"F0.wireOp",EDGE,"E0.bottom"),sQuery(id+"F0.wireOp",EDGE,"E0.top"),sQuery(id+"F0.wireOp",EDGE,"E0.left"),sQuery(id+"F0.wireOp",EDGE,"E0.right"),sQuery(id+"F0.wireOp",EDGE,"E12"),sQuery(id+"F0.wireOp",EDGE,"E13"),sQuery(id+"F0.wireOp",EDGE,"E14"),sQuery(id+"F0.wireOp",EDGE,"E15")])]}),"instanceName":"1"}),"instanceName":"1"}),"instanceName":"1"}),"instanceName":"1"});
            transform(context, id + "F36", {"entities" : qUnion([Q0]), "transformType" : TransformType.TRANSLATION_3D, "dx" : 0 * mm, "dy" : 0 * mm, "dz" : 0 * mm, "makeCopy" : true});
        }
        {
            var Q0;
            Q0=makeQuery(id+"F5.opPattern","COPY",BODY,{"derivedFrom":makeQuery(id+"F4.opPattern","COPY",BODY,{"derivedFrom":makeQuery(id+"F3.opPattern","COPY",BODY,{"derivedFrom":makeQuery(id+"F2.opPattern","COPY",BODY,{"derivedFrom":makeQuery(id+"F1.opExtrude","SWEPT_BODY",BODY,{"disambiguationData":[OSD([sQuery(id+"F0.wireOp",EDGE,"E0.bottom"),sQuery(id+"F0.wireOp",EDGE,"E0.top"),sQuery(id+"F0.wireOp",EDGE,"E0.left"),sQuery(id+"F0.wireOp",EDGE,"E0.right"),sQuery(id+"F0.wireOp",EDGE,"E12"),sQuery(id+"F0.wireOp",EDGE,"E13"),sQuery(id+"F0.wireOp",EDGE,"E14"),sQuery(id+"F0.wireOp",EDGE,"E15")])]}),"instanceName":"1"}),"instanceName":"1"}),"instanceName":"1"}),"instanceName":"1"});
            var Q1;
            Q1=makeQuery(id+"F35.opBoolean","SPLIT",BODY,{"disambiguationData":[OD(0.0)],"derivedFrom":makeQuery(id+"F33.opBoolean","SPLIT",BODY,{"disambiguationData":[OD(0.0)],"derivedFrom":makeQuery(id+"F31.opBoolean","SPLIT",BODY,{"disambiguationData":[OD(0.0)],"derivedFrom":makeQuery(id+"F29.opExtrude","SWEPT_BODY",BODY,{"disambiguationData":[OSD([sQuery(id+"F9.wireOp",EDGE,"E18"),sQuery(id+"F9.wireOp",EDGE,"E22")])]})})})});
            var Q2;
            Q2=makeQuery(id+"F35.opBoolean","SPLIT",BODY,{"disambiguationData":[OD(0.0)],"derivedFrom":makeQuery(id+"F33.opBoolean","SPLIT",BODY,{"disambiguationData":[OD(0.0)],"derivedFrom":makeQuery(id+"F31.opBoolean","SPLIT",BODY,{"disambiguationData":[OD(0.0)],"derivedFrom":makeQuery(id+"F29.opExtrude","SWEPT_BODY",BODY,{"disambiguationData":[OSD([sQuery(id+"F9.wireOp",EDGE,"E19"),sQuery(id+"F9.wireOp",EDGE,"E23")])]})})})});
            booleanBodies(context, id + "F37", {"operationType" : BooleanOperationType.SUBTRACTION, "tools" : qUnion([Q0]), "targets" : qUnion([Q1, Q2])});
        }
        {
            var Q0;
            Q0=makeQuery(id+"F4.opPattern","COPY",BODY,{"derivedFrom":makeQuery(id+"F3.opPattern","COPY",BODY,{"derivedFrom":makeQuery(id+"F2.opPattern","COPY",BODY,{"derivedFrom":makeQuery(id+"F1.opExtrude","SWEPT_BODY",BODY,{"disambiguationData":[OSD([sQuery(id+"F0.wireOp",EDGE,"E0.bottom"),sQuery(id+"F0.wireOp",EDGE,"E0.top"),sQuery(id+"F0.wireOp",EDGE,"E0.left"),sQuery(id+"F0.wireOp",EDGE,"E0.right"),sQuery(id+"F0.wireOp",EDGE,"E12"),sQuery(id+"F0.wireOp",EDGE,"E13"),sQuery(id+"F0.wireOp",EDGE,"E14"),sQuery(id+"F0.wireOp",EDGE,"E15")])]}),"instanceName":"1"}),"instanceName":"1"}),"instanceName":"1"});
            transform(context, id + "F38", {"entities" : qUnion([Q0]), "transformType" : TransformType.TRANSLATION_3D, "dx" : 0 * mm, "dy" : 0 * mm, "dz" : 0 * mm, "makeCopy" : true});
        }
        {
            var Q0;
            Q0=makeQuery(id+"F4.opPattern","COPY",BODY,{"derivedFrom":makeQuery(id+"F3.opPattern","COPY",BODY,{"derivedFrom":makeQuery(id+"F2.opPattern","COPY",BODY,{"derivedFrom":makeQuery(id+"F1.opExtrude","SWEPT_BODY",BODY,{"disambiguationData":[OSD([sQuery(id+"F0.wireOp",EDGE,"E0.bottom"),sQuery(id+"F0.wireOp",EDGE,"E0.top"),sQuery(id+"F0.wireOp",EDGE,"E0.left"),sQuery(id+"F0.wireOp",EDGE,"E0.right"),sQuery(id+"F0.wireOp",EDGE,"E12"),sQuery(id+"F0.wireOp",EDGE,"E13"),sQuery(id+"F0.wireOp",EDGE,"E14"),sQuery(id+"F0.wireOp",EDGE,"E15")])]}),"instanceName":"1"}),"instanceName":"1"}),"instanceName":"1"});
            var Q1;
            Q1=makeQuery(id+"F37.opBoolean","SPLIT",BODY,{"disambiguationData":[OD(1.0)],"derivedFrom":makeQuery(id+"F35.opBoolean","SPLIT",BODY,{"disambiguationData":[OD(0.0)],"derivedFrom":makeQuery(id+"F33.opBoolean","SPLIT",BODY,{"disambiguationData":[OD(0.0)],"derivedFrom":makeQuery(id+"F31.opBoolean","SPLIT",BODY,{"disambiguationData":[OD(0.0)],"derivedFrom":makeQuery(id+"F29.opExtrude","SWEPT_BODY",BODY,{"disambiguationData":[OSD([sQuery(id+"F9.wireOp",EDGE,"E19"),sQuery(id+"F9.wireOp",EDGE,"E23")])]})})})})});
            var Q2;
            Q2=makeQuery(id+"F37.opBoolean","SPLIT",BODY,{"disambiguationData":[OD(1.0)],"derivedFrom":makeQuery(id+"F35.opBoolean","SPLIT",BODY,{"disambiguationData":[OD(0.0)],"derivedFrom":makeQuery(id+"F33.opBoolean","SPLIT",BODY,{"disambiguationData":[OD(0.0)],"derivedFrom":makeQuery(id+"F31.opBoolean","SPLIT",BODY,{"disambiguationData":[OD(0.0)],"derivedFrom":makeQuery(id+"F29.opExtrude","SWEPT_BODY",BODY,{"disambiguationData":[OSD([sQuery(id+"F9.wireOp",EDGE,"E18"),sQuery(id+"F9.wireOp",EDGE,"E22")])]})})})})});
            booleanBodies(context, id + "F39", {"operationType" : BooleanOperationType.SUBTRACTION, "tools" : qUnion([Q0]), "targets" : qUnion([Q1, Q2])});
        }
        {
            var Q0;
            Q0=makeQuery(id+"F6.opPattern","COPY",BODY,{"derivedFrom":makeQuery(id+"F5.opPattern","COPY",BODY,{"derivedFrom":makeQuery(id+"F4.opPattern","COPY",BODY,{"derivedFrom":makeQuery(id+"F3.opPattern","COPY",BODY,{"derivedFrom":makeQuery(id+"F2.opPattern","COPY",BODY,{"derivedFrom":makeQuery(id+"F1.opExtrude","SWEPT_BODY",BODY,{"disambiguationData":[OSD([sQuery(id+"F0.wireOp",EDGE,"E0.bottom"),sQuery(id+"F0.wireOp",EDGE,"E0.top"),sQuery(id+"F0.wireOp",EDGE,"E0.left"),sQuery(id+"F0.wireOp",EDGE,"E0.right"),sQuery(id+"F0.wireOp",EDGE,"E12"),sQuery(id+"F0.wireOp",EDGE,"E13"),sQuery(id+"F0.wireOp",EDGE,"E14"),sQuery(id+"F0.wireOp",EDGE,"E15")])]}),"instanceName":"1"}),"instanceName":"1"}),"instanceName":"1"}),"instanceName":"1"}),"instanceName":"1"});
            transform(context, id + "F40", {"entities" : qUnion([Q0]), "transformType" : TransformType.TRANSLATION_3D, "dx" : 0 * mm, "dy" : 0 * mm, "dz" : 0 * mm, "makeCopy" : true});
        }
        {
            var Q0;
            Q0=makeQuery(id+"F6.opPattern","COPY",BODY,{"derivedFrom":makeQuery(id+"F5.opPattern","COPY",BODY,{"derivedFrom":makeQuery(id+"F4.opPattern","COPY",BODY,{"derivedFrom":makeQuery(id+"F3.opPattern","COPY",BODY,{"derivedFrom":makeQuery(id+"F2.opPattern","COPY",BODY,{"derivedFrom":makeQuery(id+"F1.opExtrude","SWEPT_BODY",BODY,{"disambiguationData":[OSD([sQuery(id+"F0.wireOp",EDGE,"E0.bottom"),sQuery(id+"F0.wireOp",EDGE,"E0.top"),sQuery(id+"F0.wireOp",EDGE,"E0.left"),sQuery(id+"F0.wireOp",EDGE,"E0.right"),sQuery(id+"F0.wireOp",EDGE,"E12"),sQuery(id+"F0.wireOp",EDGE,"E13"),sQuery(id+"F0.wireOp",EDGE,"E14"),sQuery(id+"F0.wireOp",EDGE,"E15")])]}),"instanceName":"1"}),"instanceName":"1"}),"instanceName":"1"}),"instanceName":"1"}),"instanceName":"1"});
            var Q1;
            Q1=makeQuery(id+"F37.opBoolean","SPLIT",BODY,{"disambiguationData":[OD(0.0)],"derivedFrom":makeQuery(id+"F35.opBoolean","SPLIT",BODY,{"disambiguationData":[OD(0.0)],"derivedFrom":makeQuery(id+"F33.opBoolean","SPLIT",BODY,{"disambiguationData":[OD(0.0)],"derivedFrom":makeQuery(id+"F31.opBoolean","SPLIT",BODY,{"disambiguationData":[OD(0.0)],"derivedFrom":makeQuery(id+"F29.opExtrude","SWEPT_BODY",BODY,{"disambiguationData":[OSD([sQuery(id+"F9.wireOp",EDGE,"E18"),sQuery(id+"F9.wireOp",EDGE,"E22")])]})})})})});
            var Q2;
            Q2=makeQuery(id+"F37.opBoolean","SPLIT",BODY,{"disambiguationData":[OD(0.0)],"derivedFrom":makeQuery(id+"F35.opBoolean","SPLIT",BODY,{"disambiguationData":[OD(0.0)],"derivedFrom":makeQuery(id+"F33.opBoolean","SPLIT",BODY,{"disambiguationData":[OD(0.0)],"derivedFrom":makeQuery(id+"F31.opBoolean","SPLIT",BODY,{"disambiguationData":[OD(0.0)],"derivedFrom":makeQuery(id+"F29.opExtrude","SWEPT_BODY",BODY,{"disambiguationData":[OSD([sQuery(id+"F9.wireOp",EDGE,"E19"),sQuery(id+"F9.wireOp",EDGE,"E23")])]})})})})});
            booleanBodies(context, id + "F41", {"operationType" : BooleanOperationType.SUBTRACTION, "tools" : qUnion([Q0]), "targets" : qUnion([Q1, Q2])});
        }
        {
            var Q0;
            Q0=makeQuery(id+"F7.opPattern","COPY",BODY,{"derivedFrom":makeQuery(id+"F6.opPattern","COPY",BODY,{"derivedFrom":makeQuery(id+"F5.opPattern","COPY",BODY,{"derivedFrom":makeQuery(id+"F4.opPattern","COPY",BODY,{"derivedFrom":makeQuery(id+"F3.opPattern","COPY",BODY,{"derivedFrom":makeQuery(id+"F2.opPattern","COPY",BODY,{"derivedFrom":makeQuery(id+"F1.opExtrude","SWEPT_BODY",BODY,{"disambiguationData":[OSD([sQuery(id+"F0.wireOp",EDGE,"E0.bottom"),sQuery(id+"F0.wireOp",EDGE,"E0.top"),sQuery(id+"F0.wireOp",EDGE,"E0.left"),sQuery(id+"F0.wireOp",EDGE,"E0.right"),sQuery(id+"F0.wireOp",EDGE,"E12"),sQuery(id+"F0.wireOp",EDGE,"E13"),sQuery(id+"F0.wireOp",EDGE,"E14"),sQuery(id+"F0.wireOp",EDGE,"E15")])]}),"instanceName":"1"}),"instanceName":"1"}),"instanceName":"1"}),"instanceName":"1"}),"instanceName":"1"}),"instanceName":"1"});
            transform(context, id + "F42", {"entities" : qUnion([Q0]), "transformType" : TransformType.TRANSLATION_3D, "dx" : 0 * mm, "dy" : 0 * mm, "dz" : 0 * mm, "makeCopy" : true});
        }
        {
            var Q0;
            Q0=makeQuery(id+"F7.opPattern","COPY",BODY,{"derivedFrom":makeQuery(id+"F6.opPattern","COPY",BODY,{"derivedFrom":makeQuery(id+"F5.opPattern","COPY",BODY,{"derivedFrom":makeQuery(id+"F4.opPattern","COPY",BODY,{"derivedFrom":makeQuery(id+"F3.opPattern","COPY",BODY,{"derivedFrom":makeQuery(id+"F2.opPattern","COPY",BODY,{"derivedFrom":makeQuery(id+"F1.opExtrude","SWEPT_BODY",BODY,{"disambiguationData":[OSD([sQuery(id+"F0.wireOp",EDGE,"E0.bottom"),sQuery(id+"F0.wireOp",EDGE,"E0.top"),sQuery(id+"F0.wireOp",EDGE,"E0.left"),sQuery(id+"F0.wireOp",EDGE,"E0.right"),sQuery(id+"F0.wireOp",EDGE,"E12"),sQuery(id+"F0.wireOp",EDGE,"E13"),sQuery(id+"F0.wireOp",EDGE,"E14"),sQuery(id+"F0.wireOp",EDGE,"E15")])]}),"instanceName":"1"}),"instanceName":"1"}),"instanceName":"1"}),"instanceName":"1"}),"instanceName":"1"}),"instanceName":"1"});
            var Q1;
            Q1=makeQuery(id+"F41.opBoolean","SPLIT",BODY,{"disambiguationData":[OD(0.0)],"derivedFrom":makeQuery(id+"F37.opBoolean","SPLIT",BODY,{"disambiguationData":[OD(0.0)],"derivedFrom":makeQuery(id+"F35.opBoolean","SPLIT",BODY,{"disambiguationData":[OD(0.0)],"derivedFrom":makeQuery(id+"F33.opBoolean","SPLIT",BODY,{"disambiguationData":[OD(0.0)],"derivedFrom":makeQuery(id+"F31.opBoolean","SPLIT",BODY,{"disambiguationData":[OD(0.0)],"derivedFrom":makeQuery(id+"F29.opExtrude","SWEPT_BODY",BODY,{"disambiguationData":[OSD([sQuery(id+"F9.wireOp",EDGE,"E19"),sQuery(id+"F9.wireOp",EDGE,"E23")])]})})})})})});
            var Q2;
            Q2=makeQuery(id+"F41.opBoolean","SPLIT",BODY,{"disambiguationData":[OD(0.0)],"derivedFrom":makeQuery(id+"F37.opBoolean","SPLIT",BODY,{"disambiguationData":[OD(0.0)],"derivedFrom":makeQuery(id+"F35.opBoolean","SPLIT",BODY,{"disambiguationData":[OD(0.0)],"derivedFrom":makeQuery(id+"F33.opBoolean","SPLIT",BODY,{"disambiguationData":[OD(0.0)],"derivedFrom":makeQuery(id+"F31.opBoolean","SPLIT",BODY,{"disambiguationData":[OD(0.0)],"derivedFrom":makeQuery(id+"F29.opExtrude","SWEPT_BODY",BODY,{"disambiguationData":[OSD([sQuery(id+"F9.wireOp",EDGE,"E18"),sQuery(id+"F9.wireOp",EDGE,"E22")])]})})})})})});
            booleanBodies(context, id + "F43", {"operationType" : BooleanOperationType.SUBTRACTION, "tools" : qUnion([Q0]), "targets" : qUnion([Q1, Q2])});
        }
        {
            var Q0;
            Q0=makeQuery(id+"F8.opPattern","COPY",BODY,{"derivedFrom":makeQuery(id+"F7.opPattern","COPY",BODY,{"derivedFrom":makeQuery(id+"F6.opPattern","COPY",BODY,{"derivedFrom":makeQuery(id+"F5.opPattern","COPY",BODY,{"derivedFrom":makeQuery(id+"F4.opPattern","COPY",BODY,{"derivedFrom":makeQuery(id+"F3.opPattern","COPY",BODY,{"derivedFrom":makeQuery(id+"F2.opPattern","COPY",BODY,{"derivedFrom":makeQuery(id+"F1.opExtrude","SWEPT_BODY",BODY,{"disambiguationData":[OSD([sQuery(id+"F0.wireOp",EDGE,"E0.bottom"),sQuery(id+"F0.wireOp",EDGE,"E0.top"),sQuery(id+"F0.wireOp",EDGE,"E0.left"),sQuery(id+"F0.wireOp",EDGE,"E0.right"),sQuery(id+"F0.wireOp",EDGE,"E12"),sQuery(id+"F0.wireOp",EDGE,"E13"),sQuery(id+"F0.wireOp",EDGE,"E14"),sQuery(id+"F0.wireOp",EDGE,"E15")])]}),"instanceName":"1"}),"instanceName":"1"}),"instanceName":"1"}),"instanceName":"1"}),"instanceName":"1"}),"instanceName":"1"}),"instanceName":"1"});
            transform(context, id + "F44", {"entities" : qUnion([Q0]), "transformType" : TransformType.TRANSLATION_3D, "dx" : 0 * mm, "dy" : 0 * mm, "dz" : 0 * mm, "makeCopy" : true});
        }
        {
            var Q0;
            Q0=makeQuery(id+"F8.opPattern","COPY",BODY,{"derivedFrom":makeQuery(id+"F7.opPattern","COPY",BODY,{"derivedFrom":makeQuery(id+"F6.opPattern","COPY",BODY,{"derivedFrom":makeQuery(id+"F5.opPattern","COPY",BODY,{"derivedFrom":makeQuery(id+"F4.opPattern","COPY",BODY,{"derivedFrom":makeQuery(id+"F3.opPattern","COPY",BODY,{"derivedFrom":makeQuery(id+"F2.opPattern","COPY",BODY,{"derivedFrom":makeQuery(id+"F1.opExtrude","SWEPT_BODY",BODY,{"disambiguationData":[OSD([sQuery(id+"F0.wireOp",EDGE,"E0.bottom"),sQuery(id+"F0.wireOp",EDGE,"E0.top"),sQuery(id+"F0.wireOp",EDGE,"E0.left"),sQuery(id+"F0.wireOp",EDGE,"E0.right"),sQuery(id+"F0.wireOp",EDGE,"E12"),sQuery(id+"F0.wireOp",EDGE,"E13"),sQuery(id+"F0.wireOp",EDGE,"E14"),sQuery(id+"F0.wireOp",EDGE,"E15")])]}),"instanceName":"1"}),"instanceName":"1"}),"instanceName":"1"}),"instanceName":"1"}),"instanceName":"1"}),"instanceName":"1"}),"instanceName":"1"});
            var Q1;
            Q1=makeQuery(id+"F43.opBoolean","SPLIT",BODY,{"disambiguationData":[OD(0.0)],"derivedFrom":makeQuery(id+"F41.opBoolean","SPLIT",BODY,{"disambiguationData":[OD(0.0)],"derivedFrom":makeQuery(id+"F37.opBoolean","SPLIT",BODY,{"disambiguationData":[OD(0.0)],"derivedFrom":makeQuery(id+"F35.opBoolean","SPLIT",BODY,{"disambiguationData":[OD(0.0)],"derivedFrom":makeQuery(id+"F33.opBoolean","SPLIT",BODY,{"disambiguationData":[OD(0.0)],"derivedFrom":makeQuery(id+"F31.opBoolean","SPLIT",BODY,{"disambiguationData":[OD(0.0)],"derivedFrom":makeQuery(id+"F29.opExtrude","SWEPT_BODY",BODY,{"disambiguationData":[OSD([sQuery(id+"F9.wireOp",EDGE,"E18"),sQuery(id+"F9.wireOp",EDGE,"E22")])]})})})})})})});
            var Q2;
            Q2=makeQuery(id+"F43.opBoolean","SPLIT",BODY,{"disambiguationData":[OD(0.0)],"derivedFrom":makeQuery(id+"F41.opBoolean","SPLIT",BODY,{"disambiguationData":[OD(0.0)],"derivedFrom":makeQuery(id+"F37.opBoolean","SPLIT",BODY,{"disambiguationData":[OD(0.0)],"derivedFrom":makeQuery(id+"F35.opBoolean","SPLIT",BODY,{"disambiguationData":[OD(0.0)],"derivedFrom":makeQuery(id+"F33.opBoolean","SPLIT",BODY,{"disambiguationData":[OD(0.0)],"derivedFrom":makeQuery(id+"F31.opBoolean","SPLIT",BODY,{"disambiguationData":[OD(0.0)],"derivedFrom":makeQuery(id+"F29.opExtrude","SWEPT_BODY",BODY,{"disambiguationData":[OSD([sQuery(id+"F9.wireOp",EDGE,"E19"),sQuery(id+"F9.wireOp",EDGE,"E23")])]})})})})})})});
            booleanBodies(context, id + "F45", {"operationType" : BooleanOperationType.SUBTRACTION, "tools" : qUnion([Q0]), "targets" : qUnion([Q1, Q2])});
        }
        {
            var Q0;
            Q0=makeQuery(id+"F9.imprint","IMPRINT",FACE,{"disambiguationData":[TD([[makeQuery(id+"F9.imprint","IMPRINT",EDGE,{"derivedFrom":sQuery(id+"F9.wireOp",EDGE,"E24")}),1.0]])]});
            var Q1;
            Q1=makeQuery(id+"F9.imprint","IMPRINT",FACE,{"disambiguationData":[TD([[makeQuery(id+"F9.imprint","IMPRINT",EDGE,{"derivedFrom":sQuery(id+"F9.wireOp",EDGE,"E25")}),1.0]])]});
            var Q2;
            Q2=sQuery(id+"F9.wireOp",EDGE,"E26");
            var Q3;
            Q3=sQuery(id+"F9.wireOp",EDGE,"E27");
            extrude(context, id + "F46", {"entities" : qUnion([Q0, Q1]), "surfaceEntities" : qUnion([Q2, Q3]), "depth" : 203.2 * mm, "hasSecondDirection" : true, "secondDirectionOppositeDirection" : true, "secondDirectionDepth" : 469.9 * mm});
        }
        {
            var Q0;
            Q0=makeQuery(id+"F9.imprint","IMPRINT",FACE,{"disambiguationData":[TD([[makeQuery(id+"F9.imprint","IMPRINT",EDGE,{"derivedFrom":sQuery(id+"F9.wireOp",EDGE,"E27")}),1.0]])]});
            var Q1;
            Q1=makeQuery(id+"F9.imprint","IMPRINT",FACE,{"disambiguationData":[TD([[makeQuery(id+"F9.imprint","IMPRINT",EDGE,{"derivedFrom":sQuery(id+"F9.wireOp",EDGE,"E26")}),1.0]])]});
            var Q2;
            Q2=sQuery(id+"F9.wireOp",EDGE,"E24");
            var Q3;
            Q3=sQuery(id+"F9.wireOp",EDGE,"E25");
            extrude(context, id + "F47", {"entities" : qUnion([Q0, Q1]), "surfaceEntities" : qUnion([Q2, Q3]), "depth" : 101.6 * mm, "hasSecondDirection" : true, "secondDirectionOppositeDirection" : true, "secondDirectionDepth" : 571.5 * mm});
        }
        {
            var Q0;
            Q0=makeQuery(id+"F30.opPattern","COPY",FACE,{"derivedFrom":makeQuery(id+"F11.opPattern","COPY",FACE,{"derivedFrom":makeQuery(id+"F1.opExtrude","SWEPT_FACE",FACE,{"disambiguationData":[OSD([sQuery(id+"F0.wireOp",EDGE,"E0.right")])]}),"instanceName":"1"}),"instanceName":"1"});
            var sketch = newSketch(context, id + "F48", { "sketchPlane" : qUnion([Q0])});
            skLineSegment(sketch, "E28.bottom", {"start": v(-292.3, 38.1) * mm, "end": v(317.3, 38.1) * mm});
            skLineSegment(sketch, "E28.top", {"start": v(-292.3, 76.2) * mm, "end": v(317.3, 76.2) * mm});
            skLineSegment(sketch, "E28.left", {"start": v(-292.3, 38.1) * mm, "end": v(-292.3, 76.2) * mm, "construction": true});
            skLineSegment(sketch, "E28.right", {"start": v(317.3, 38.1) * mm, "end": v(317.3, 76.2) * mm, "construction": true});
            skLineSegment(sketch, "E29", {"start": v(-292.3, 38.1) * mm, "end": v(-292.3, 12.7) * mm, "construction": true});
            skLineSegment(sketch, "E30", {"start": v(317.3, 38.1) * mm, "end": v(317.3, 12.7) * mm, "construction": true});
            skLineSegment(sketch, "E31", {"start": v(-292.3, 76.2) * mm, "end": v(-368.5, 76.2) * mm});
            skLineSegment(sketch, "E32", {"start": v(-368.5, 76.2) * mm, "end": v(-368.5, 38.1) * mm});
            skLineSegment(sketch, "E33", {"start": v(-368.5, 38.1) * mm, "end": v(-292.3, 38.1) * mm});
            skLineSegment(sketch, "E34", {"start": v(317.3, 76.2) * mm, "end": v(393.5, 76.2) * mm});
            skLineSegment(sketch, "E35", {"start": v(393.5, 76.2) * mm, "end": v(393.5, 38.1) * mm});
            skLineSegment(sketch, "E36", {"start": v(393.5, 38.1) * mm, "end": v(317.3, 38.1) * mm});
            skSolve(sketch);
        }
        {
            var Q0;
            Q0 = qSketchRegion(id + "F48", true);
            extrude(context, id + "F49", {"entities" : qUnion([Q0]), "depth" : 88.9 * mm});
        }
        {
            var Q0;
            Q0=makeQuery(id+"F49.opExtrude","SWEPT_BODY",BODY,{"disambiguationData":[OSD([sQuery(id+"F48.wireOp",EDGE,"E28.bottom"),sQuery(id+"F48.wireOp",EDGE,"E28.top"),sQuery(id+"F48.wireOp",EDGE,"E31"),sQuery(id+"F48.wireOp",EDGE,"E32"),sQuery(id+"F48.wireOp",EDGE,"E33"),sQuery(id+"F48.wireOp",EDGE,"E34"),sQuery(id+"F48.wireOp",EDGE,"E35"),sQuery(id+"F48.wireOp",EDGE,"E36")])]});
            transform(context, id + "F50", {"entities" : qUnion([Q0]), "transformType" : TransformType.TRANSLATION_3D, "dx" : -95.25 * mm, "dy" : 0 * mm, "dz" : 0 * mm, "makeCopy" : false});
        }
        {
            var Q0;
            Q0=makeQuery(id+"F47.opExtrude","SWEPT_BODY",BODY,{"disambiguationData":[OSD([sQuery(id+"F9.wireOp",EDGE,"E26")])]});
            transform(context, id + "F51", {"entities" : qUnion([Q0]), "transformType" : TransformType.TRANSLATION_3D, "dx" : 0 * mm, "dy" : 0 * mm, "dz" : 0 * mm, "makeCopy" : true});
        }
        {
            var Q0;
            Q0=makeQuery(id+"F47.opExtrude","SWEPT_BODY",BODY,{"disambiguationData":[OSD([sQuery(id+"F9.wireOp",EDGE,"E27")])]});
            transform(context, id + "F52", {"entities" : qUnion([Q0]), "transformType" : TransformType.TRANSLATION_3D, "dx" : 0 * mm, "dy" : 0 * mm, "dz" : 0 * mm, "makeCopy" : true});
        }
        {
            var Q0;
            Q0=makeQuery(id+"F47.opExtrude","SWEPT_BODY",BODY,{"disambiguationData":[OSD([sQuery(id+"F9.wireOp",EDGE,"E26")])]});
            var Q1;
            Q1=makeQuery(id+"F47.opExtrude","SWEPT_BODY",BODY,{"disambiguationData":[OSD([sQuery(id+"F9.wireOp",EDGE,"E27")])]});
            var Q2;
            Q2=makeQuery(id+"F49.opExtrude","SWEPT_BODY",BODY,{"disambiguationData":[OSD([sQuery(id+"F48.wireOp",EDGE,"E28.bottom"),sQuery(id+"F48.wireOp",EDGE,"E28.top"),sQuery(id+"F48.wireOp",EDGE,"E31"),sQuery(id+"F48.wireOp",EDGE,"E32"),sQuery(id+"F48.wireOp",EDGE,"E33"),sQuery(id+"F48.wireOp",EDGE,"E34"),sQuery(id+"F48.wireOp",EDGE,"E35"),sQuery(id+"F48.wireOp",EDGE,"E36")])]});
            booleanBodies(context, id + "F53", {"operationType" : BooleanOperationType.SUBTRACTION, "tools" : qUnion([Q0, Q1]), "targets" : qUnion([Q2])});
        }
        {
            var Q0;
            Q0=makeQuery(id+"F49.opExtrude","SWEPT_BODY",BODY,{"disambiguationData":[OSD([sQuery(id+"F48.wireOp",EDGE,"E28.bottom"),sQuery(id+"F48.wireOp",EDGE,"E28.top"),sQuery(id+"F48.wireOp",EDGE,"E31"),sQuery(id+"F48.wireOp",EDGE,"E32"),sQuery(id+"F48.wireOp",EDGE,"E33"),sQuery(id+"F48.wireOp",EDGE,"E34"),sQuery(id+"F48.wireOp",EDGE,"E35"),sQuery(id+"F48.wireOp",EDGE,"E36")])]});
            transform(context, id + "F54", {"entities" : qUnion([Q0]), "transformType" : TransformType.TRANSLATION_3D, "dx" : 0 * mm, "dy" : 0 * mm, "dz" : -558.8 * mm, "makeCopy" : true});
        }
        {
            var Q0;
            Q0=makeQuery(id+"F49.opExtrude","SWEPT_BODY",BODY,{"disambiguationData":[OSD([sQuery(id+"F48.wireOp",EDGE,"E28.bottom"),sQuery(id+"F48.wireOp",EDGE,"E28.top"),sQuery(id+"F48.wireOp",EDGE,"E31"),sQuery(id+"F48.wireOp",EDGE,"E32"),sQuery(id+"F48.wireOp",EDGE,"E33"),sQuery(id+"F48.wireOp",EDGE,"E34"),sQuery(id+"F48.wireOp",EDGE,"E35"),sQuery(id+"F48.wireOp",EDGE,"E36")])]});
            transform(context, id + "F55", {"entities" : qUnion([Q0]), "transformType" : TransformType.TRANSLATION_3D, "dx" : -1117.6 * mm, "dy" : 0 * mm, "dz" : 101.6 * mm, "makeCopy" : true});
        }
        {
            var Q0;
            Q0=makeQuery(id+"F55.opPattern","COPY",BODY,{"derivedFrom":makeQuery(id+"F49.opExtrude","SWEPT_BODY",BODY,{"disambiguationData":[OSD([sQuery(id+"F48.wireOp",EDGE,"E28.bottom"),sQuery(id+"F48.wireOp",EDGE,"E28.top"),sQuery(id+"F48.wireOp",EDGE,"E31"),sQuery(id+"F48.wireOp",EDGE,"E32"),sQuery(id+"F48.wireOp",EDGE,"E33"),sQuery(id+"F48.wireOp",EDGE,"E34"),sQuery(id+"F48.wireOp",EDGE,"E35"),sQuery(id+"F48.wireOp",EDGE,"E36")])]}),"instanceName":"1"});
            transform(context, id + "F56", {"entities" : qUnion([Q0]), "transformType" : TransformType.TRANSLATION_3D, "dx" : 0 * mm, "dy" : 0 * mm, "dz" : -558.8 * mm, "makeCopy" : true});
        }
        {
            var Q0;
            Q0=makeQuery(id+"F49.opExtrude","CAP_FACE",FACE,{"disambiguationData":[OSD([sQuery(id+"F48.wireOp",EDGE,"E28.bottom"),sQuery(id+"F48.wireOp",EDGE,"E28.top"),sQuery(id+"F48.wireOp",EDGE,"E31"),sQuery(id+"F48.wireOp",EDGE,"E32"),sQuery(id+"F48.wireOp",EDGE,"E33"),sQuery(id+"F48.wireOp",EDGE,"E34"),sQuery(id+"F48.wireOp",EDGE,"E35"),sQuery(id+"F48.wireOp",EDGE,"E36")])],"isStart":false});
            var sketch = newSketch(context, id + "F57", { "sketchPlane" : qUnion([Q0])});
            skLineSegment(sketch, "E37.bottom", {"start": v(-368.5, 38.1) * mm, "end": v(-330.4, 38.1) * mm});
            skLineSegment(sketch, "E37.top", {"start": v(-368.5, -482.6) * mm, "end": v(-330.4, -482.6) * mm});
            skLineSegment(sketch, "E37.left", {"start": v(-368.5, 38.1) * mm, "end": v(-368.5, -482.6) * mm});
            skLineSegment(sketch, "E37.right", {"start": v(-330.4, 38.1) * mm, "end": v(-330.4, -482.6) * mm});
            skLineSegment(sketch, "E38.0", {"start": v(-368.5, -482.6) * mm, "end": v(393.5, -482.6) * mm, "construction": true});
            skLineSegment(sketch, "E39.bottom", {"start": v(393.5, 38.1) * mm, "end": v(355.4, 38.1) * mm});
            skLineSegment(sketch, "E39.top", {"start": v(393.5, -482.6) * mm, "end": v(355.4, -482.6) * mm});
            skLineSegment(sketch, "E39.left", {"start": v(393.5, 38.1) * mm, "end": v(393.5, -482.6) * mm});
            skLineSegment(sketch, "E39.right", {"start": v(355.4, 38.1) * mm, "end": v(355.4, -482.6) * mm});
            skSolve(sketch);
        }
        {
            var Q0;
            Q0 = qSketchRegion(id + "F57", true);
            var Q1;
            Q1=makeQuery(id+"F49.opExtrude","CAP_FACE",FACE,{"disambiguationData":[OSD([sQuery(id+"F48.wireOp",EDGE,"E28.bottom"),sQuery(id+"F48.wireOp",EDGE,"E28.top"),sQuery(id+"F48.wireOp",EDGE,"E31"),sQuery(id+"F48.wireOp",EDGE,"E32"),sQuery(id+"F48.wireOp",EDGE,"E33"),sQuery(id+"F48.wireOp",EDGE,"E34"),sQuery(id+"F48.wireOp",EDGE,"E35"),sQuery(id+"F48.wireOp",EDGE,"E36")])],"isStart":true});
            extrude(context, id + "F58", {"entities" : qUnion([Q0]), "operationType" : NewBodyOperationType.ADD, "endBound" : BoundingType.UP_TO_SURFACE, "oppositeDirection" : true, "endBoundEntityFace" : qUnion([Q1]), "depth" : 25.4 * mm});
        }
        {
            var Q0;
            Q0=makeQuery(id+"F55.opPattern","COPY",FACE,{"derivedFrom":makeQuery(id+"F49.opExtrude","CAP_FACE",FACE,{"disambiguationData":[OSD([sQuery(id+"F48.wireOp",EDGE,"E28.bottom"),sQuery(id+"F48.wireOp",EDGE,"E28.top"),sQuery(id+"F48.wireOp",EDGE,"E31"),sQuery(id+"F48.wireOp",EDGE,"E32"),sQuery(id+"F48.wireOp",EDGE,"E33"),sQuery(id+"F48.wireOp",EDGE,"E34"),sQuery(id+"F48.wireOp",EDGE,"E35"),sQuery(id+"F48.wireOp",EDGE,"E36")])],"isStart":true}),"instanceName":"1"});
            var sketch = newSketch(context, id + "F59", { "sketchPlane" : qUnion([Q0])});
            skLineSegment(sketch, "E40.bottom", {"start": v(-393.5, 139.7) * mm, "end": v(-355.4, 139.7) * mm});
            skLineSegment(sketch, "E40.top", {"start": v(-393.5, -381) * mm, "end": v(-355.4, -381) * mm});
            skLineSegment(sketch, "E40.left", {"start": v(-393.5, 139.7) * mm, "end": v(-393.5, -381) * mm});
            skLineSegment(sketch, "E40.right", {"start": v(-355.4, 139.7) * mm, "end": v(-355.4, -381) * mm});
            skLineSegment(sketch, "E41.bottom", {"start": v(368.5, 139.7) * mm, "end": v(330.4, 139.7) * mm});
            skLineSegment(sketch, "E41.top", {"start": v(368.5, -381) * mm, "end": v(330.4, -381) * mm});
            skLineSegment(sketch, "E41.left", {"start": v(368.5, 139.7) * mm, "end": v(368.5, -381) * mm});
            skLineSegment(sketch, "E41.right", {"start": v(330.4, 139.7) * mm, "end": v(330.4, -381) * mm});
            skLineSegment(sketch, "E42.0", {"start": v(368.5, -381) * mm, "end": v(-393.5, -381) * mm});
            skSolve(sketch);
        }
        {
            var Q0;
            Q0 = qSketchRegion(id + "F59", true);
            var Q1;
            Q1=makeQuery(id+"F55.opPattern","COPY",FACE,{"derivedFrom":makeQuery(id+"F49.opExtrude","CAP_FACE",FACE,{"disambiguationData":[OSD([sQuery(id+"F48.wireOp",EDGE,"E28.bottom"),sQuery(id+"F48.wireOp",EDGE,"E28.top"),sQuery(id+"F48.wireOp",EDGE,"E31"),sQuery(id+"F48.wireOp",EDGE,"E32"),sQuery(id+"F48.wireOp",EDGE,"E33"),sQuery(id+"F48.wireOp",EDGE,"E34"),sQuery(id+"F48.wireOp",EDGE,"E35"),sQuery(id+"F48.wireOp",EDGE,"E36")])],"isStart":false}),"instanceName":"1"});
            extrude(context, id + "F60", {"entities" : qUnion([Q0]), "operationType" : NewBodyOperationType.ADD, "endBound" : BoundingType.UP_TO_SURFACE, "oppositeDirection" : true, "endBoundEntityFace" : qUnion([Q1]), "depth" : 25.4 * mm});
        }
        {
            var Q0;
            {var subQ0=sQuery(id+"F59.wireOp",EDGE,"E42.0");var subQ1=makeQuery(id+"F55.opPattern","COPY",FACE,{"derivedFrom":makeQuery(id+"F49.opExtrude","CAP_FACE",FACE,{"disambiguationData":[OSD([sQuery(id+"F48.wireOp",EDGE,"E28.bottom"),sQuery(id+"F48.wireOp",EDGE,"E28.top"),sQuery(id+"F48.wireOp",EDGE,"E31"),sQuery(id+"F48.wireOp",EDGE,"E32"),sQuery(id+"F48.wireOp",EDGE,"E33"),sQuery(id+"F48.wireOp",EDGE,"E34"),sQuery(id+"F48.wireOp",EDGE,"E35"),sQuery(id+"F48.wireOp",EDGE,"E36")])],"isStart":true}),"instanceName":"1"});Q0=makeQuery(id+"F60.boolean.opBoolean","MERGE",FACE,{"derivedFrom":[subQ1,makeQuery(id+"F56.opPattern","COPY",FACE,{"derivedFrom":subQ1,"instanceName":"1"}),makeQuery(id+"F60.opExtrude","CAP_FACE",FACE,{"disambiguationData":[OSD([sQuery(id+"F59.wireOp",EDGE,"E40.bottom"),sQuery(id+"F59.wireOp",EDGE,"E40.left"),sQuery(id+"F59.wireOp",EDGE,"E40.right"),subQ0])],"isStart":true}),makeQuery(id+"F60.opExtrude","CAP_FACE",FACE,{"disambiguationData":[OSD([sQuery(id+"F59.wireOp",EDGE,"E41.bottom"),sQuery(id+"F59.wireOp",EDGE,"E41.left"),sQuery(id+"F59.wireOp",EDGE,"E41.right"),subQ0])],"isStart":true})]});}
            var sketch = newSketch(context, id + "F61", { "sketchPlane" : qUnion([Q0])});
            skLineSegment(sketch, "E43", {"start": v(-393.5, 177.8) * mm, "end": v(-355.4, 177.8) * mm, "construction": true});
            skLineSegment(sketch, "E44", {"start": v(-355.4, 177.8) * mm, "end": v(-355.4, 317.5) * mm});
            skLineSegment(sketch, "E45", {"start": v(-355.4, 317.5) * mm, "end": v(-126.8, 317.5) * mm});
            skLineSegment(sketch, "E46", {"start": v(-126.8, 317.5) * mm, "end": v(-126.8, 177.8) * mm});
            skLineSegment(sketch, "E47", {"start": v(-355.4, 177.8) * mm, "end": v(-317.3, 177.8) * mm});
            skLineSegment(sketch, "E48", {"start": v(-317.3, 177.8) * mm, "end": v(-317.3, 279.4) * mm});
            skLineSegment(sketch, "E49", {"start": v(-317.3, 279.4) * mm, "end": v(-164.9, 279.4) * mm});
            skLineSegment(sketch, "E50", {"start": v(-164.9, 279.4) * mm, "end": v(-164.9, 177.8) * mm});
            skLineSegment(sketch, "E51", {"start": v(-164.9, 177.8) * mm, "end": v(-126.8, 177.8) * mm});
            skLineSegment(sketch, "E52", {"start": v(-317.3, 279.4) * mm, "end": v(-317.3, 317.5) * mm, "construction": true});
            skLineSegment(sketch, "E53", {"start": v(368.5, 177.8) * mm, "end": v(330.4, 177.8) * mm, "construction": true});
            skLineSegment(sketch, "E54", {"start": v(330.4, 177.8) * mm, "end": v(330.4, 317.5) * mm});
            skLineSegment(sketch, "E55", {"start": v(330.4, 317.5) * mm, "end": v(101.8, 317.5) * mm});
            skLineSegment(sketch, "E56", {"start": v(101.8, 317.5) * mm, "end": v(101.8, 177.8) * mm});
            skLineSegment(sketch, "E57", {"start": v(101.8, 177.8) * mm, "end": v(-126.8, 177.8) * mm, "construction": true});
            skLineSegment(sketch, "E58", {"start": v(101.8, 177.8) * mm, "end": v(139.9, 177.8) * mm});
            skLineSegment(sketch, "E59", {"start": v(139.9, 177.8) * mm, "end": v(139.9, 279.4) * mm});
            skLineSegment(sketch, "E60", {"start": v(139.9, 279.4) * mm, "end": v(292.3, 279.4) * mm});
            skLineSegment(sketch, "E61", {"start": v(292.3, 279.4) * mm, "end": v(292.3, 177.8) * mm});
            skLineSegment(sketch, "E62", {"start": v(292.3, 177.8) * mm, "end": v(330.4, 177.8) * mm});
            skLineSegment(sketch, "E63.0", {"start": v(-250.62, 215.9) * mm, "end": v(-231.57, 215.9) * mm});
            skLineSegment(sketch, "E64", {"start": v(-241.1, 215.9) * mm, "end": v(-241.1, 279.4) * mm, "construction": true});
            skSolve(sketch);
        }
        {
            var Q0;
            Q0 = qSketchRegion(id + "F61", true);
            var Q1;
            {var subQ0=sQuery(id+"F59.wireOp",EDGE,"E42.0");var subQ1=makeQuery(id+"F55.opPattern","COPY",FACE,{"derivedFrom":makeQuery(id+"F49.opExtrude","CAP_FACE",FACE,{"disambiguationData":[OSD([sQuery(id+"F48.wireOp",EDGE,"E28.bottom"),sQuery(id+"F48.wireOp",EDGE,"E28.top"),sQuery(id+"F48.wireOp",EDGE,"E31"),sQuery(id+"F48.wireOp",EDGE,"E32"),sQuery(id+"F48.wireOp",EDGE,"E33"),sQuery(id+"F48.wireOp",EDGE,"E34"),sQuery(id+"F48.wireOp",EDGE,"E35"),sQuery(id+"F48.wireOp",EDGE,"E36")])],"isStart":false}),"instanceName":"1"});Q1=makeQuery(id+"F60.boolean.opBoolean","MERGE",FACE,{"derivedFrom":[subQ1,makeQuery(id+"F56.opPattern","COPY",FACE,{"derivedFrom":subQ1,"instanceName":"1"}),makeQuery(id+"F60.opExtrude","CAP_FACE",FACE,{"disambiguationData":[OSD([sQuery(id+"F59.wireOp",EDGE,"E40.bottom"),sQuery(id+"F59.wireOp",EDGE,"E40.left"),sQuery(id+"F59.wireOp",EDGE,"E40.right"),subQ0])],"isStart":false}),makeQuery(id+"F60.opExtrude","CAP_FACE",FACE,{"disambiguationData":[OSD([sQuery(id+"F59.wireOp",EDGE,"E41.bottom"),sQuery(id+"F59.wireOp",EDGE,"E41.left"),sQuery(id+"F59.wireOp",EDGE,"E41.right"),subQ0])],"isStart":false})]});}
            extrude(context, id + "F62", {"entities" : qUnion([Q0]), "operationType" : NewBodyOperationType.ADD, "endBound" : BoundingType.UP_TO_SURFACE, "oppositeDirection" : true, "endBoundEntityFace" : qUnion([Q1]), "depth" : 25.4 * mm});
        }
        {
            var Q0;
            {var subQ0=makeQuery(id+"F49.opExtrude","CAP_FACE",FACE,{"disambiguationData":[OSD([sQuery(id+"F48.wireOp",EDGE,"E28.bottom"),sQuery(id+"F48.wireOp",EDGE,"E28.top"),sQuery(id+"F48.wireOp",EDGE,"E31"),sQuery(id+"F48.wireOp",EDGE,"E32"),sQuery(id+"F48.wireOp",EDGE,"E33"),sQuery(id+"F48.wireOp",EDGE,"E34"),sQuery(id+"F48.wireOp",EDGE,"E35"),sQuery(id+"F48.wireOp",EDGE,"E36")])],"isStart":false});Q0=makeQuery(id+"F58.boolean.opBoolean","MERGE",FACE,{"derivedFrom":[subQ0,makeQuery(id+"F54.opPattern","COPY",FACE,{"derivedFrom":subQ0,"instanceName":"1"}),makeQuery(id+"F58.opExtrude","CAP_FACE",FACE,{"disambiguationData":[OSD([sQuery(id+"F57.wireOp",EDGE,"E37.bottom"),sQuery(id+"F57.wireOp",EDGE,"E37.top"),sQuery(id+"F57.wireOp",EDGE,"E37.left"),sQuery(id+"F57.wireOp",EDGE,"E37.right")])],"isStart":true}),makeQuery(id+"F58.opExtrude","CAP_FACE",FACE,{"disambiguationData":[OSD([sQuery(id+"F57.wireOp",EDGE,"E39.bottom"),sQuery(id+"F57.wireOp",EDGE,"E39.top"),sQuery(id+"F57.wireOp",EDGE,"E39.left"),sQuery(id+"F57.wireOp",EDGE,"E39.right")])],"isStart":true})]});}
            var sketch = newSketch(context, id + "F63", { "sketchPlane" : qUnion([Q0])});
            skLineSegment(sketch, "E65", {"start": v(-368.5, -520.7) * mm, "end": v(-317.4, -520.7) * mm, "construction": true});
            skLineSegment(sketch, "E66", {"start": v(-317.4, -520.7) * mm, "end": v(-317.4, -673.1) * mm});
            skLineSegment(sketch, "E67", {"start": v(-317.4, -673.1) * mm, "end": v(-304.7, -673.1) * mm});
            skLineSegment(sketch, "E68", {"start": v(-304.7, -673.1) * mm, "end": v(-304.7, -533.4) * mm});
            skLineSegment(sketch, "E69", {"start": v(-304.7, -533.4) * mm, "end": v(-266.6, -533.4) * mm});
            skLineSegment(sketch, "E70", {"start": v(-266.6, -533.4) * mm, "end": v(-266.6, -673.1) * mm});
            skLineSegment(sketch, "E71", {"start": v(-266.6, -673.1) * mm, "end": v(-253.9, -673.1) * mm});
            skLineSegment(sketch, "E72", {"start": v(-253.9, -673.1) * mm, "end": v(-253.9, -520.7) * mm});
            skLineSegment(sketch, "E73", {"start": v(-253.9, -520.7) * mm, "end": v(-317.4, -520.7) * mm});
            skLineSegment(sketch, "E74", {"start": v(393.5, -520.7) * mm, "end": v(330.64, -520.7) * mm, "construction": true});
            skLineSegment(sketch, "E75", {"start": v(330.64, -520.7) * mm, "end": v(330.64, -673.1) * mm});
            skLineSegment(sketch, "E76", {"start": v(330.64, -673.1) * mm, "end": v(317.94, -673.1) * mm});
            skLineSegment(sketch, "E77", {"start": v(317.94, -673.1) * mm, "end": v(317.94, -533.4) * mm});
            skLineSegment(sketch, "E78", {"start": v(317.94, -533.4) * mm, "end": v(279.84, -533.4) * mm});
            skLineSegment(sketch, "E79", {"start": v(279.84, -533.4) * mm, "end": v(279.84, -673.1) * mm});
            skLineSegment(sketch, "E80", {"start": v(279.84, -673.1) * mm, "end": v(267.14, -673.1) * mm});
            skLineSegment(sketch, "E81", {"start": v(267.14, -673.1) * mm, "end": v(267.14, -520.7) * mm});
            skLineSegment(sketch, "E82", {"start": v(267.14, -520.7) * mm, "end": v(330.64, -520.7) * mm});
            skLineSegment(sketch, "E83", {"start": v(-304.7, -533.4) * mm, "end": v(-304.7, -520.7) * mm, "construction": true});
            skSolve(sketch);
        }
        {
            var Q0;
            Q0 = qSketchRegion(id + "F63", true);
            var Q1;
            {var subQ0=makeQuery(id+"F49.opExtrude","CAP_FACE",FACE,{"disambiguationData":[OSD([sQuery(id+"F48.wireOp",EDGE,"E28.bottom"),sQuery(id+"F48.wireOp",EDGE,"E28.top"),sQuery(id+"F48.wireOp",EDGE,"E31"),sQuery(id+"F48.wireOp",EDGE,"E32"),sQuery(id+"F48.wireOp",EDGE,"E33"),sQuery(id+"F48.wireOp",EDGE,"E34"),sQuery(id+"F48.wireOp",EDGE,"E35"),sQuery(id+"F48.wireOp",EDGE,"E36")])],"isStart":true});Q1=makeQuery(id+"F58.boolean.opBoolean","MERGE",FACE,{"derivedFrom":[subQ0,makeQuery(id+"F54.opPattern","COPY",FACE,{"derivedFrom":subQ0,"instanceName":"1"}),makeQuery(id+"F58.opExtrude","CAP_FACE",FACE,{"disambiguationData":[OSD([sQuery(id+"F57.wireOp",EDGE,"E37.bottom"),sQuery(id+"F57.wireOp",EDGE,"E37.top"),sQuery(id+"F57.wireOp",EDGE,"E37.left"),sQuery(id+"F57.wireOp",EDGE,"E37.right")])],"isStart":false}),makeQuery(id+"F58.opExtrude","CAP_FACE",FACE,{"disambiguationData":[OSD([sQuery(id+"F57.wireOp",EDGE,"E39.bottom"),sQuery(id+"F57.wireOp",EDGE,"E39.top"),sQuery(id+"F57.wireOp",EDGE,"E39.left"),sQuery(id+"F57.wireOp",EDGE,"E39.right")])],"isStart":false})]});}
            extrude(context, id + "F64", {"entities" : qUnion([Q0]), "endBound" : BoundingType.UP_TO_SURFACE, "oppositeDirection" : true, "endBoundEntityFace" : qUnion([Q1]), "depth" : 25.4 * mm});
        }
        {
            var Q0;
            Q0=makeQuery(id+"F64.opExtrude","SWEPT_FACE",FACE,{"disambiguationData":[OSD([sQuery(id+"F63.wireOp",EDGE,"E66")])]});
            var sketch = newSketch(context, id + "F65", { "sketchPlane" : qUnion([Q0])});
            skLineSegment(sketch, "E84", {"start": v(515.49, -520.7) * mm, "end": v(515.49, -596.9) * mm, "construction": true});
            skLineSegment(sketch, "E85", {"start": v(515.49, -596.9) * mm, "end": v(515.49, -673.1) * mm});
            skLineSegment(sketch, "E86", {"start": v(604.39, -520.7) * mm, "end": v(604.39, -596.9) * mm, "construction": true});
            skLineSegment(sketch, "E87", {"start": v(604.39, -596.9) * mm, "end": v(604.39, -673.1) * mm});
            skArc(sketch, "E88", {"start": v(515.49, -596.9) * mm, "mid": v(559.94, -641.35) * mm, "end": v(604.39, -596.9) * mm});
            skSolve(sketch);
        }
        {
            var Q0;
            {var subQ0=sQuery(id+"F65.wireOp",EDGE,"E85");Q0=makeQuery(id+"F65.imprint","IMPRINT",FACE,{"disambiguationData":[TD([[makeQuery(id+"F65.imprint","IMPRINT",EDGE,{"derivedFrom":subQ0}),-1.0]])]});}
            var Q1;
            {var subQ0=sQuery(id+"F65.wireOp",EDGE,"E87");Q1=makeQuery(id+"F65.imprint","IMPRINT",FACE,{"disambiguationData":[TD([[makeQuery(id+"F65.imprint","IMPRINT",EDGE,{"derivedFrom":subQ0}),-1.0]])]});}
            extrude(context, id + "F66", {"entities" : qUnion([Q0, Q1]), "operationType" : NewBodyOperationType.REMOVE, "endBound" : BoundingType.THROUGH_ALL, "oppositeDirection" : true, "depth" : 25.4 * mm});
        }
        {
            var Q0;
            Q0=makeQuery(id+"F64.opExtrude","SWEPT_FACE",FACE,{"disambiguationData":[OSD([sQuery(id+"F63.wireOp",EDGE,"E70")])]});
            var sketch = newSketch(context, id + "F67", { "sketchPlane" : qUnion([Q0])});
            skCircle(sketch, "E89", {"center": v(559.94, -596.9) * mm, "radius": 60.33 * mm});
            skSolve(sketch);
        }
        {
            var Q0;
            Q0 = qSketchRegion(id + "F67", true);
            var Q1;
            Q1=makeQuery(id+"F64.opExtrude","SWEPT_FACE",FACE,{"disambiguationData":[OSD([sQuery(id+"F63.wireOp",EDGE,"E68")])]});
            extrude(context, id + "F68", {"entities" : qUnion([Q0]), "endBound" : BoundingType.UP_TO_SURFACE, "endBoundEntityFace" : qUnion([Q1]), "depth" : 25.4 * mm});
        }
        {
            var Q0;
            Q0=makeQuery(id+"F68.opExtrude","SWEPT_FACE",FACE,{"disambiguationData":[OSD([sQuery(id+"F67.wireOp",EDGE,"E89")])]});
            fillet(context, id + "F69", {"entities" : qUnion([Q0]), "radius" : 12.7 * mm, "tangentPropagation" : true, "allowEdgeOverflow" : false});
        }
        {
            var Q0;
            Q0=makeQuery(id+"F68.opExtrude","SWEPT_BODY",BODY,{"disambiguationData":[OSD([sQuery(id+"F67.wireOp",EDGE,"E89")])]});
            transform(context, id + "F70", {"entities" : qUnion([Q0]), "transformType" : TransformType.TRANSLATION_3D, "dx" : 0 * mm, "dy" : 584.5 * mm, "dz" : 0 * mm, "makeCopy" : true});
        }
        {
            var Q0;
            {var subQ1=sQuery(id+"F48.wireOp",EDGE,"E35");var subQ2=makeQuery(id+"F55.opPattern","COPY",FACE,{"derivedFrom":makeQuery(id+"F49.opExtrude","SWEPT_FACE",FACE,{"disambiguationData":[OSD([subQ1])]}),"instanceName":"1"});var subQ8=sQuery(id+"F48.wireOp",EDGE,"E34");var subQ11=sQuery(id+"F48.wireOp",EDGE,"E31");var subQ12=sQuery(id+"F48.wireOp",EDGE,"E28.top");Q0=makeQuery(id+"F62.boolean.opBoolean","SPLIT",FACE,{"disambiguationData":[TD([subQ2])],"derivedFrom":makeQuery(id+"F55.opPattern","COPY",FACE,{"derivedFrom":makeQuery(id+"F49.opExtrude","SWEPT_FACE",FACE,{"disambiguationData":[OSD([subQ12,subQ11,subQ8])]}),"instanceName":"1"})});}
            var sketch = newSketch(context, id + "F71", { "sketchPlane" : qUnion([Q0])});
            skCircle(sketch, "E90.0", {"center": v(-557.66, 241.1) * mm, "radius": 9.53 * mm});
            skCircle(sketch, "E90.1", {"center": v(-557.66, -216.1) * mm, "radius": 9.53 * mm});
            skLineSegment(sketch, "E91", {"start": v(-557.66, 241.1) * mm, "end": v(-575.03, 241.1) * mm, "construction": true});
            skLineSegment(sketch, "E92", {"start": v(-557.66, 241.1) * mm, "end": v(-540.3, 241.1) * mm, "construction": true});
            skLineSegment(sketch, "E93", {"start": v(-575.03, 241.1) * mm, "end": v(-567.19, 258.46) * mm});
            skLineSegment(sketch, "E94", {"start": v(-567.19, 258.46) * mm, "end": v(-548.14, 258.46) * mm});
            skLineSegment(sketch, "E95", {"start": v(-548.14, 258.46) * mm, "end": v(-540.3, 241.1) * mm});
            skLineSegment(sketch, "E96", {"start": v(-540.3, 241.1) * mm, "end": v(-548.14, 223.74) * mm});
            skLineSegment(sketch, "E97", {"start": v(-548.14, 223.74) * mm, "end": v(-567.19, 223.74) * mm});
            skLineSegment(sketch, "E98", {"start": v(-567.19, 223.74) * mm, "end": v(-575.03, 241.1) * mm});
            skLineSegment(sketch, "E99", {"start": v(-557.66, 258.46) * mm, "end": v(-557.66, 241.1) * mm, "construction": true});
            skLineSegment(sketch, "E100", {"start": v(-557.66, 223.74) * mm, "end": v(-557.66, 241.1) * mm, "construction": true});
            skLineSegment(sketch, "E101", {"start": v(-575.03, -216.1) * mm, "end": v(-567.19, -198.74) * mm});
            skLineSegment(sketch, "E102", {"start": v(-567.19, -198.74) * mm, "end": v(-548.14, -198.74) * mm});
            skLineSegment(sketch, "E103", {"start": v(-548.14, -198.74) * mm, "end": v(-540.3, -216.1) * mm});
            skLineSegment(sketch, "E104", {"start": v(-540.3, -216.1) * mm, "end": v(-548.14, -233.46) * mm});
            skLineSegment(sketch, "E105", {"start": v(-548.14, -233.46) * mm, "end": v(-567.19, -233.46) * mm});
            skLineSegment(sketch, "E106", {"start": v(-567.19, -233.46) * mm, "end": v(-575.03, -216.1) * mm});
            skLineSegment(sketch, "E107", {"start": v(-575.03, 241.1) * mm, "end": v(-575.03, -216.1) * mm, "construction": true});
            skLineSegment(sketch, "E108", {"start": v(-557.66, -216.1) * mm, "end": v(-575.03, -216.1) * mm, "construction": true});
            skLineSegment(sketch, "E109", {"start": v(-557.66, -198.74) * mm, "end": v(-557.66, -216.1) * mm, "construction": true});
            skLineSegment(sketch, "E110", {"start": v(-557.66, -216.1) * mm, "end": v(-540.3, -216.1) * mm, "construction": true});
            skSolve(sketch);
        }
        {
            var Q0;
            Q0 = qSketchRegion(id + "F71", true);
            extrude(context, id + "F72", {"entities" : qUnion([Q0]), "depth" : 25.4 * mm});
        }
        {
            var Q0;
            Q0=makeQuery(id+"F72.opExtrude","SWEPT_BODY",BODY,{"disambiguationData":[OSD([sQuery(id+"F71.wireOp",EDGE,"E90.0"),sQuery(id+"F71.wireOp",EDGE,"E93"),sQuery(id+"F71.wireOp",EDGE,"E94"),sQuery(id+"F71.wireOp",EDGE,"E95"),sQuery(id+"F71.wireOp",EDGE,"E96"),sQuery(id+"F71.wireOp",EDGE,"E97"),sQuery(id+"F71.wireOp",EDGE,"E98")])]});
            transform(context, id + "F73", {"entities" : qUnion([Q0]), "transformType" : TransformType.TRANSLATION_3D, "dx" : 0 * mm, "dy" : 0 * mm, "dz" : -622.3 * mm, "makeCopy" : true});
        }
        {
            var Q0;
            Q0=makeQuery(id+"F46.opExtrude","SWEPT_BODY",BODY,{"disambiguationData":[OSD([sQuery(id+"F9.wireOp",EDGE,"E24")])]});
            transform(context, id + "F74", {"entities" : qUnion([Q0]), "transformType" : TransformType.TRANSLATION_3D, "dx" : 0 * mm, "dy" : 0 * mm, "dz" : 0 * mm, "makeCopy" : true});
        }
        {
            var Q0;
            Q0=makeQuery(id+"F46.opExtrude","SWEPT_BODY",BODY,{"disambiguationData":[OSD([sQuery(id+"F9.wireOp",EDGE,"E24")])]});
            var Q1;
            Q1=makeQuery(id+"F73.opPattern","COPY",BODY,{"derivedFrom":makeQuery(id+"F72.opExtrude","SWEPT_BODY",BODY,{"disambiguationData":[OSD([sQuery(id+"F71.wireOp",EDGE,"E90.0"),sQuery(id+"F71.wireOp",EDGE,"E93"),sQuery(id+"F71.wireOp",EDGE,"E94"),sQuery(id+"F71.wireOp",EDGE,"E95"),sQuery(id+"F71.wireOp",EDGE,"E96"),sQuery(id+"F71.wireOp",EDGE,"E97"),sQuery(id+"F71.wireOp",EDGE,"E98")])]}),"instanceName":"1"});
            var Q2;
            Q2=makeQuery(id+"F72.opExtrude","SWEPT_BODY",BODY,{"disambiguationData":[OSD([sQuery(id+"F71.wireOp",EDGE,"E90.0"),sQuery(id+"F71.wireOp",EDGE,"E93"),sQuery(id+"F71.wireOp",EDGE,"E94"),sQuery(id+"F71.wireOp",EDGE,"E95"),sQuery(id+"F71.wireOp",EDGE,"E96"),sQuery(id+"F71.wireOp",EDGE,"E97"),sQuery(id+"F71.wireOp",EDGE,"E98")])]});
            booleanBodies(context, id + "F75", {"operationType" : BooleanOperationType.SUBTRACTION, "tools" : qUnion([Q0]), "targets" : qUnion([Q1, Q2])});
        }
        {
            var Q0;
            Q0=makeQuery(id+"F72.opExtrude","SWEPT_BODY",BODY,{"disambiguationData":[OSD([sQuery(id+"F71.wireOp",EDGE,"E90.1"),sQuery(id+"F71.wireOp",EDGE,"E101"),sQuery(id+"F71.wireOp",EDGE,"E102"),sQuery(id+"F71.wireOp",EDGE,"E103"),sQuery(id+"F71.wireOp",EDGE,"E104"),sQuery(id+"F71.wireOp",EDGE,"E105"),sQuery(id+"F71.wireOp",EDGE,"E106")])]});
            transform(context, id + "F76", {"entities" : qUnion([Q0]), "transformType" : TransformType.TRANSLATION_3D, "dx" : 0 * mm, "dy" : 0 * mm, "dz" : -622.3 * mm, "makeCopy" : true});
        }
        {
            var Q0;
            Q0=makeQuery(id+"F46.opExtrude","SWEPT_BODY",BODY,{"disambiguationData":[OSD([sQuery(id+"F9.wireOp",EDGE,"E25")])]});
            transform(context, id + "F77", {"entities" : qUnion([Q0]), "transformType" : TransformType.TRANSLATION_3D, "dx" : 0 * mm, "dy" : 0 * mm, "dz" : 0 * mm, "makeCopy" : true});
        }
        {
            var Q0;
            Q0=makeQuery(id+"F46.opExtrude","SWEPT_BODY",BODY,{"disambiguationData":[OSD([sQuery(id+"F9.wireOp",EDGE,"E25")])]});
            var Q1;
            Q1=makeQuery(id+"F76.opPattern","COPY",BODY,{"derivedFrom":makeQuery(id+"F72.opExtrude","SWEPT_BODY",BODY,{"disambiguationData":[OSD([sQuery(id+"F71.wireOp",EDGE,"E90.1"),sQuery(id+"F71.wireOp",EDGE,"E101"),sQuery(id+"F71.wireOp",EDGE,"E102"),sQuery(id+"F71.wireOp",EDGE,"E103"),sQuery(id+"F71.wireOp",EDGE,"E104"),sQuery(id+"F71.wireOp",EDGE,"E105"),sQuery(id+"F71.wireOp",EDGE,"E106")])]}),"instanceName":"1"});
            var Q2;
            Q2=makeQuery(id+"F72.opExtrude","SWEPT_BODY",BODY,{"disambiguationData":[OSD([sQuery(id+"F71.wireOp",EDGE,"E90.1"),sQuery(id+"F71.wireOp",EDGE,"E101"),sQuery(id+"F71.wireOp",EDGE,"E102"),sQuery(id+"F71.wireOp",EDGE,"E103"),sQuery(id+"F71.wireOp",EDGE,"E104"),sQuery(id+"F71.wireOp",EDGE,"E105"),sQuery(id+"F71.wireOp",EDGE,"E106")])]});
            booleanBodies(context, id + "F78", {"operationType" : BooleanOperationType.SUBTRACTION, "tools" : qUnion([Q0]), "targets" : qUnion([Q1, Q2])});
        }
        {
            var Q0;
            Q0=makeQuery(id+"F72.opExtrude","SWEPT_BODY",BODY,{"disambiguationData":[OSD([sQuery(id+"F71.wireOp",EDGE,"E90.1"),sQuery(id+"F71.wireOp",EDGE,"E101"),sQuery(id+"F71.wireOp",EDGE,"E102"),sQuery(id+"F71.wireOp",EDGE,"E103"),sQuery(id+"F71.wireOp",EDGE,"E104"),sQuery(id+"F71.wireOp",EDGE,"E105"),sQuery(id+"F71.wireOp",EDGE,"E106")])]});
            transform(context, id + "F79", {"entities" : qUnion([Q0]), "transformType" : TransformType.TRANSLATION_3D, "dx" : 1117.6 * mm, "dy" : 0 * mm, "dz" : -101.6 * mm, "makeCopy" : true});
        }
        {
            var Q0;
            Q0=makeQuery(id+"F79.opPattern","COPY",BODY,{"derivedFrom":makeQuery(id+"F72.opExtrude","SWEPT_BODY",BODY,{"disambiguationData":[OSD([sQuery(id+"F71.wireOp",EDGE,"E90.1"),sQuery(id+"F71.wireOp",EDGE,"E101"),sQuery(id+"F71.wireOp",EDGE,"E102"),sQuery(id+"F71.wireOp",EDGE,"E103"),sQuery(id+"F71.wireOp",EDGE,"E104"),sQuery(id+"F71.wireOp",EDGE,"E105"),sQuery(id+"F71.wireOp",EDGE,"E106")])]}),"instanceName":"1"});
            transform(context, id + "F80", {"entities" : qUnion([Q0]), "transformType" : TransformType.TRANSLATION_3D, "dx" : 0 * mm, "dy" : 457.2 * mm, "dz" : 0 * mm, "makeCopy" : true});
        }
        {
            var Q0;
            Q0=makeQuery(id+"F79.opPattern","COPY",BODY,{"derivedFrom":makeQuery(id+"F72.opExtrude","SWEPT_BODY",BODY,{"disambiguationData":[OSD([sQuery(id+"F71.wireOp",EDGE,"E90.1"),sQuery(id+"F71.wireOp",EDGE,"E101"),sQuery(id+"F71.wireOp",EDGE,"E102"),sQuery(id+"F71.wireOp",EDGE,"E103"),sQuery(id+"F71.wireOp",EDGE,"E104"),sQuery(id+"F71.wireOp",EDGE,"E105"),sQuery(id+"F71.wireOp",EDGE,"E106")])]}),"instanceName":"1"});
            transform(context, id + "F81", {"entities" : qUnion([Q0]), "transformType" : TransformType.TRANSLATION_3D, "dx" : 0 * mm, "dy" : 0 * mm, "dz" : -622.3 * mm, "makeCopy" : true});
        }
        {
            var Q0;
            Q0=makeQuery(id+"F80.opPattern","COPY",BODY,{"derivedFrom":makeQuery(id+"F79.opPattern","COPY",BODY,{"derivedFrom":makeQuery(id+"F72.opExtrude","SWEPT_BODY",BODY,{"disambiguationData":[OSD([sQuery(id+"F71.wireOp",EDGE,"E90.1"),sQuery(id+"F71.wireOp",EDGE,"E101"),sQuery(id+"F71.wireOp",EDGE,"E102"),sQuery(id+"F71.wireOp",EDGE,"E103"),sQuery(id+"F71.wireOp",EDGE,"E104"),sQuery(id+"F71.wireOp",EDGE,"E105"),sQuery(id+"F71.wireOp",EDGE,"E106")])]}),"instanceName":"1"}),"instanceName":"1"});
            transform(context, id + "F82", {"entities" : qUnion([Q0]), "transformType" : TransformType.TRANSLATION_3D, "dx" : 0 * mm, "dy" : 0 * mm, "dz" : -622.3 * mm, "makeCopy" : true});
        }
        {
            var Q0;
            {var subQ0=makeQuery(id+"F49.opExtrude","CAP_FACE",FACE,{"disambiguationData":[OSD([sQuery(id+"F48.wireOp",EDGE,"E28.bottom"),sQuery(id+"F48.wireOp",EDGE,"E28.top"),sQuery(id+"F48.wireOp",EDGE,"E31"),sQuery(id+"F48.wireOp",EDGE,"E32"),sQuery(id+"F48.wireOp",EDGE,"E33"),sQuery(id+"F48.wireOp",EDGE,"E34"),sQuery(id+"F48.wireOp",EDGE,"E35"),sQuery(id+"F48.wireOp",EDGE,"E36")])],"isStart":false});Q0=makeQuery(id+"F58.boolean.opBoolean","MERGE",FACE,{"derivedFrom":[subQ0,makeQuery(id+"F54.opPattern","COPY",FACE,{"derivedFrom":subQ0,"instanceName":"1"}),makeQuery(id+"F58.opExtrude","CAP_FACE",FACE,{"disambiguationData":[OSD([sQuery(id+"F57.wireOp",EDGE,"E37.bottom"),sQuery(id+"F57.wireOp",EDGE,"E37.top"),sQuery(id+"F57.wireOp",EDGE,"E37.left"),sQuery(id+"F57.wireOp",EDGE,"E37.right")])],"isStart":true}),makeQuery(id+"F58.opExtrude","CAP_FACE",FACE,{"disambiguationData":[OSD([sQuery(id+"F57.wireOp",EDGE,"E39.bottom"),sQuery(id+"F57.wireOp",EDGE,"E39.top"),sQuery(id+"F57.wireOp",EDGE,"E39.left"),sQuery(id+"F57.wireOp",EDGE,"E39.right")])],"isStart":true})]});}
            var sketch = newSketch(context, id + "F83", { "sketchPlane" : qUnion([Q0])});
            skLineSegment(sketch, "E111.0", {"start": v(-368.5, 177.8) * mm, "end": v(-330.4, 177.8) * mm, "construction": true});
            skLineSegment(sketch, "E112", {"start": v(-368.5, 76.2) * mm, "end": v(-330.4, 76.2) * mm, "construction": true});
            skLineSegment(sketch, "E113", {"start": v(-330.4, 76.2) * mm, "end": v(-330.4, 215.9) * mm});
            skLineSegment(sketch, "E114.1", {"start": v(-330.4, 177.8) * mm, "end": v(-330.4, 317.5) * mm, "construction": true});
            skLineSegment(sketch, "E114.2", {"start": v(-330.4, 317.5) * mm, "end": v(-101.8, 317.5) * mm, "construction": true});
            skLineSegment(sketch, "E114.3", {"start": v(-292.3, 279.4) * mm, "end": v(-292.3, 177.8) * mm, "construction": true});
            skLineSegment(sketch, "E114.4", {"start": v(-139.9, 279.4) * mm, "end": v(-292.3, 279.4) * mm, "construction": true});
            skLineSegment(sketch, "E114.5", {"start": v(-139.9, 177.8) * mm, "end": v(-139.9, 279.4) * mm, "construction": true});
            skLineSegment(sketch, "E114.6", {"start": v(-292.3, 177.8) * mm, "end": v(-139.9, 177.8) * mm, "construction": true});
            skLineSegment(sketch, "E114.7", {"start": v(-101.8, 317.5) * mm, "end": v(-101.8, 177.8) * mm, "construction": true});
            skLineSegment(sketch, "E114.8", {"start": v(-101.8, 177.8) * mm, "end": v(126.8, 177.8) * mm, "construction": true});
            skLineSegment(sketch, "E115", {"start": v(-330.4, 215.9) * mm, "end": v(-101.8, 215.9) * mm});
            skLineSegment(sketch, "E116", {"start": v(-101.8, 215.9) * mm, "end": v(-101.8, 76.2) * mm});
            skLineSegment(sketch, "E117", {"start": v(-101.8, 76.2) * mm, "end": v(126.8, 76.2) * mm});
            skLineSegment(sketch, "E118", {"start": v(126.8, 76.2) * mm, "end": v(126.8, 215.9) * mm});
            skLineSegment(sketch, "E119", {"start": v(126.8, 215.9) * mm, "end": v(355.4, 215.9) * mm});
            skLineSegment(sketch, "E120", {"start": v(355.4, 215.9) * mm, "end": v(355.4, 76.2) * mm});
            skLineSegment(sketch, "E121", {"start": v(355.4, 76.2) * mm, "end": v(393.5, 76.2) * mm, "construction": true});
            skLineSegment(sketch, "E122", {"start": v(-330.4, 76.2) * mm, "end": v(-292.3, 76.2) * mm});
            skLineSegment(sketch, "E123", {"start": v(-292.3, 76.2) * mm, "end": v(-292.3, 177.8) * mm});
            skLineSegment(sketch, "E124", {"start": v(-292.3, 177.8) * mm, "end": v(-139.9, 177.8) * mm});
            skLineSegment(sketch, "E125", {"start": v(-139.9, 177.8) * mm, "end": v(-139.9, 76.2) * mm});
            skLineSegment(sketch, "E126", {"start": v(-139.9, 76.2) * mm, "end": v(-101.8, 76.2) * mm});
            skLineSegment(sketch, "E127", {"start": v(126.8, 76.2) * mm, "end": v(164.9, 76.2) * mm});
            skLineSegment(sketch, "E128", {"start": v(164.9, 76.2) * mm, "end": v(164.9, 177.8) * mm});
            skLineSegment(sketch, "E129", {"start": v(164.9, 177.8) * mm, "end": v(317.3, 177.8) * mm});
            skLineSegment(sketch, "E130", {"start": v(317.3, 177.8) * mm, "end": v(317.3, 76.2) * mm});
            skLineSegment(sketch, "E131", {"start": v(317.3, 76.2) * mm, "end": v(355.4, 76.2) * mm});
            skSolve(sketch);
        }
        {
            var Q0;
            Q0 = qSketchRegion(id + "F83", true);
            var Q1;
            {var subQ0=makeQuery(id+"F49.opExtrude","CAP_FACE",FACE,{"disambiguationData":[OSD([sQuery(id+"F48.wireOp",EDGE,"E28.bottom"),sQuery(id+"F48.wireOp",EDGE,"E28.top"),sQuery(id+"F48.wireOp",EDGE,"E31"),sQuery(id+"F48.wireOp",EDGE,"E32"),sQuery(id+"F48.wireOp",EDGE,"E33"),sQuery(id+"F48.wireOp",EDGE,"E34"),sQuery(id+"F48.wireOp",EDGE,"E35"),sQuery(id+"F48.wireOp",EDGE,"E36")])],"isStart":true});Q1=makeQuery(id+"F58.boolean.opBoolean","MERGE",FACE,{"derivedFrom":[subQ0,makeQuery(id+"F54.opPattern","COPY",FACE,{"derivedFrom":subQ0,"instanceName":"1"}),makeQuery(id+"F58.opExtrude","CAP_FACE",FACE,{"disambiguationData":[OSD([sQuery(id+"F57.wireOp",EDGE,"E37.bottom"),sQuery(id+"F57.wireOp",EDGE,"E37.top"),sQuery(id+"F57.wireOp",EDGE,"E37.left"),sQuery(id+"F57.wireOp",EDGE,"E37.right")])],"isStart":false}),makeQuery(id+"F58.opExtrude","CAP_FACE",FACE,{"disambiguationData":[OSD([sQuery(id+"F57.wireOp",EDGE,"E39.bottom"),sQuery(id+"F57.wireOp",EDGE,"E39.top"),sQuery(id+"F57.wireOp",EDGE,"E39.left"),sQuery(id+"F57.wireOp",EDGE,"E39.right")])],"isStart":false})]});}
            extrude(context, id + "F84", {"entities" : qUnion([Q0]), "operationType" : NewBodyOperationType.ADD, "endBound" : BoundingType.UP_TO_SURFACE, "oppositeDirection" : true, "endBoundEntityFace" : qUnion([Q1]), "depth" : 25.4 * mm});
        }
        {
            var Q0;
            {var subQ0=makeQuery(id+"F49.opExtrude","CAP_FACE",FACE,{"disambiguationData":[OSD([sQuery(id+"F48.wireOp",EDGE,"E28.bottom"),sQuery(id+"F48.wireOp",EDGE,"E28.top"),sQuery(id+"F48.wireOp",EDGE,"E31"),sQuery(id+"F48.wireOp",EDGE,"E32"),sQuery(id+"F48.wireOp",EDGE,"E33"),sQuery(id+"F48.wireOp",EDGE,"E34"),sQuery(id+"F48.wireOp",EDGE,"E35"),sQuery(id+"F48.wireOp",EDGE,"E36")])],"isStart":false});Q0=makeQuery(id+"F84.boolean.opBoolean","MERGE",FACE,{"derivedFrom":[makeQuery(id+"F58.boolean.opBoolean","MERGE",FACE,{"derivedFrom":[subQ0,makeQuery(id+"F54.opPattern","COPY",FACE,{"derivedFrom":subQ0,"instanceName":"1"}),makeQuery(id+"F58.opExtrude","CAP_FACE",FACE,{"disambiguationData":[OSD([sQuery(id+"F57.wireOp",EDGE,"E37.bottom"),sQuery(id+"F57.wireOp",EDGE,"E37.top"),sQuery(id+"F57.wireOp",EDGE,"E37.left"),sQuery(id+"F57.wireOp",EDGE,"E37.right")])],"isStart":true}),makeQuery(id+"F58.opExtrude","CAP_FACE",FACE,{"disambiguationData":[OSD([sQuery(id+"F57.wireOp",EDGE,"E39.bottom"),sQuery(id+"F57.wireOp",EDGE,"E39.top"),sQuery(id+"F57.wireOp",EDGE,"E39.left"),sQuery(id+"F57.wireOp",EDGE,"E39.right")])],"isStart":true})]}),makeQuery(id+"F84.opExtrude","CAP_FACE",FACE,{"disambiguationData":[OSD([sQuery(id+"F83.wireOp",EDGE,"E113"),sQuery(id+"F83.wireOp",EDGE,"E115"),sQuery(id+"F83.wireOp",EDGE,"E116"),sQuery(id+"F83.wireOp",EDGE,"E122"),sQuery(id+"F83.wireOp",EDGE,"E123"),sQuery(id+"F83.wireOp",EDGE,"E124"),sQuery(id+"F83.wireOp",EDGE,"E125"),sQuery(id+"F83.wireOp",EDGE,"E126")])],"isStart":true}),makeQuery(id+"F84.opExtrude","CAP_FACE",FACE,{"disambiguationData":[OSD([sQuery(id+"F83.wireOp",EDGE,"E118"),sQuery(id+"F83.wireOp",EDGE,"E119"),sQuery(id+"F83.wireOp",EDGE,"E120"),sQuery(id+"F83.wireOp",EDGE,"E127"),sQuery(id+"F83.wireOp",EDGE,"E128"),sQuery(id+"F83.wireOp",EDGE,"E129"),sQuery(id+"F83.wireOp",EDGE,"E130"),sQuery(id+"F83.wireOp",EDGE,"E131")])],"isStart":true})]});}
            var sketch = newSketch(context, id + "F85", { "sketchPlane" : qUnion([Q0])});
            skLineSegment(sketch, "E132.bottom", {"start": v(-330.4, -419.1) * mm, "end": v(-266.9, -419.1) * mm});
            skLineSegment(sketch, "E132.top", {"start": v(-330.4, -482.6) * mm, "end": v(-266.9, -482.6) * mm});
            skLineSegment(sketch, "E132.left", {"start": v(-330.4, -419.1) * mm, "end": v(-330.4, -482.6) * mm});
            skLineSegment(sketch, "E132.right", {"start": v(-266.9, -419.1) * mm, "end": v(-266.9, -482.6) * mm});
            skLineSegment(sketch, "E133.bottom", {"start": v(355.4, -482.6) * mm, "end": v(291.9, -482.6) * mm});
            skLineSegment(sketch, "E133.top", {"start": v(355.4, -419.1) * mm, "end": v(291.9, -419.1) * mm});
            skLineSegment(sketch, "E133.left", {"start": v(355.4, -482.6) * mm, "end": v(355.4, -419.1) * mm});
            skLineSegment(sketch, "E133.right", {"start": v(291.9, -482.6) * mm, "end": v(291.9, -419.1) * mm});
            skLineSegment(sketch, "E134.bottom", {"start": v(-101.8, 76.2) * mm, "end": v(-38.3, 76.2) * mm});
            skLineSegment(sketch, "E134.top", {"start": v(-101.8, 139.7) * mm, "end": v(-38.3, 139.7) * mm});
            skLineSegment(sketch, "E134.left", {"start": v(-101.8, 76.2) * mm, "end": v(-101.8, 139.7) * mm});
            skLineSegment(sketch, "E134.right", {"start": v(-38.3, 76.2) * mm, "end": v(-38.3, 139.7) * mm});
            skLineSegment(sketch, "E135.bottom", {"start": v(126.8, 76.2) * mm, "end": v(63.3, 76.2) * mm});
            skLineSegment(sketch, "E135.top", {"start": v(126.8, 139.7) * mm, "end": v(63.3, 139.7) * mm});
            skLineSegment(sketch, "E135.left", {"start": v(126.8, 76.2) * mm, "end": v(126.8, 139.7) * mm});
            skLineSegment(sketch, "E135.right", {"start": v(63.3, 76.2) * mm, "end": v(63.3, 139.7) * mm});
            skSolve(sketch);
        }
        {
            var Q0;
            Q0 = qSketchRegion(id + "F85", true);
            var Q1;
            {var subQ0=sQuery(id+"F59.wireOp",EDGE,"E42.0");var subQ1=makeQuery(id+"F55.opPattern","COPY",FACE,{"derivedFrom":makeQuery(id+"F49.opExtrude","CAP_FACE",FACE,{"disambiguationData":[OSD([sQuery(id+"F48.wireOp",EDGE,"E28.bottom"),sQuery(id+"F48.wireOp",EDGE,"E28.top"),sQuery(id+"F48.wireOp",EDGE,"E31"),sQuery(id+"F48.wireOp",EDGE,"E32"),sQuery(id+"F48.wireOp",EDGE,"E33"),sQuery(id+"F48.wireOp",EDGE,"E34"),sQuery(id+"F48.wireOp",EDGE,"E35"),sQuery(id+"F48.wireOp",EDGE,"E36")])],"isStart":true}),"instanceName":"1"});Q1=makeQuery(id+"F62.boolean.opBoolean","MERGE",FACE,{"derivedFrom":[makeQuery(id+"F60.boolean.opBoolean","MERGE",FACE,{"derivedFrom":[subQ1,makeQuery(id+"F56.opPattern","COPY",FACE,{"derivedFrom":subQ1,"instanceName":"1"}),makeQuery(id+"F60.opExtrude","CAP_FACE",FACE,{"disambiguationData":[OSD([sQuery(id+"F59.wireOp",EDGE,"E40.bottom"),sQuery(id+"F59.wireOp",EDGE,"E40.left"),sQuery(id+"F59.wireOp",EDGE,"E40.right"),subQ0])],"isStart":true}),makeQuery(id+"F60.opExtrude","CAP_FACE",FACE,{"disambiguationData":[OSD([sQuery(id+"F59.wireOp",EDGE,"E41.bottom"),sQuery(id+"F59.wireOp",EDGE,"E41.left"),sQuery(id+"F59.wireOp",EDGE,"E41.right"),subQ0])],"isStart":true})]}),makeQuery(id+"F62.opExtrude","CAP_FACE",FACE,{"disambiguationData":[OSD([sQuery(id+"F61.wireOp",EDGE,"E44"),sQuery(id+"F61.wireOp",EDGE,"E45"),sQuery(id+"F61.wireOp",EDGE,"E46"),sQuery(id+"F61.wireOp",EDGE,"E47"),sQuery(id+"F61.wireOp",EDGE,"E48"),sQuery(id+"F61.wireOp",EDGE,"E49"),sQuery(id+"F61.wireOp",EDGE,"E50"),sQuery(id+"F61.wireOp",EDGE,"E51")])],"isStart":true}),makeQuery(id+"F62.opExtrude","CAP_FACE",FACE,{"disambiguationData":[OSD([sQuery(id+"F61.wireOp",EDGE,"E54"),sQuery(id+"F61.wireOp",EDGE,"E55"),sQuery(id+"F61.wireOp",EDGE,"E56"),sQuery(id+"F61.wireOp",EDGE,"E58"),sQuery(id+"F61.wireOp",EDGE,"E59"),sQuery(id+"F61.wireOp",EDGE,"E60"),sQuery(id+"F61.wireOp",EDGE,"E61"),sQuery(id+"F61.wireOp",EDGE,"E62")])],"isStart":true})]});}
            extrude(context, id + "F86", {"entities" : qUnion([Q0]), "endBound" : BoundingType.UP_TO_SURFACE, "oppositeDirection" : true, "endBoundEntityFace" : qUnion([Q1]), "depth" : 25.4 * mm});
        }
        {
            var Q0;
            {var subQ0=sQuery(id+"F59.wireOp",EDGE,"E42.0");var subQ1=makeQuery(id+"F55.opPattern","COPY",FACE,{"derivedFrom":makeQuery(id+"F49.opExtrude","CAP_FACE",FACE,{"disambiguationData":[OSD([sQuery(id+"F48.wireOp",EDGE,"E28.bottom"),sQuery(id+"F48.wireOp",EDGE,"E28.top"),sQuery(id+"F48.wireOp",EDGE,"E31"),sQuery(id+"F48.wireOp",EDGE,"E32"),sQuery(id+"F48.wireOp",EDGE,"E33"),sQuery(id+"F48.wireOp",EDGE,"E34"),sQuery(id+"F48.wireOp",EDGE,"E35"),sQuery(id+"F48.wireOp",EDGE,"E36")])],"isStart":false}),"instanceName":"1"});Q0=makeQuery(id+"F62.boolean.opBoolean","MERGE",FACE,{"derivedFrom":[makeQuery(id+"F60.boolean.opBoolean","MERGE",FACE,{"derivedFrom":[subQ1,makeQuery(id+"F56.opPattern","COPY",FACE,{"derivedFrom":subQ1,"instanceName":"1"}),makeQuery(id+"F60.opExtrude","CAP_FACE",FACE,{"disambiguationData":[OSD([sQuery(id+"F59.wireOp",EDGE,"E40.bottom"),sQuery(id+"F59.wireOp",EDGE,"E40.left"),sQuery(id+"F59.wireOp",EDGE,"E40.right"),subQ0])],"isStart":false}),makeQuery(id+"F60.opExtrude","CAP_FACE",FACE,{"disambiguationData":[OSD([sQuery(id+"F59.wireOp",EDGE,"E41.bottom"),sQuery(id+"F59.wireOp",EDGE,"E41.left"),sQuery(id+"F59.wireOp",EDGE,"E41.right"),subQ0])],"isStart":false})]}),makeQuery(id+"F62.opExtrude","CAP_FACE",FACE,{"disambiguationData":[OSD([sQuery(id+"F61.wireOp",EDGE,"E44"),sQuery(id+"F61.wireOp",EDGE,"E45"),sQuery(id+"F61.wireOp",EDGE,"E46"),sQuery(id+"F61.wireOp",EDGE,"E47"),sQuery(id+"F61.wireOp",EDGE,"E48"),sQuery(id+"F61.wireOp",EDGE,"E49"),sQuery(id+"F61.wireOp",EDGE,"E50"),sQuery(id+"F61.wireOp",EDGE,"E51")])],"isStart":false}),makeQuery(id+"F62.opExtrude","CAP_FACE",FACE,{"disambiguationData":[OSD([sQuery(id+"F61.wireOp",EDGE,"E54"),sQuery(id+"F61.wireOp",EDGE,"E55"),sQuery(id+"F61.wireOp",EDGE,"E56"),sQuery(id+"F61.wireOp",EDGE,"E58"),sQuery(id+"F61.wireOp",EDGE,"E59"),sQuery(id+"F61.wireOp",EDGE,"E60"),sQuery(id+"F61.wireOp",EDGE,"E61"),sQuery(id+"F61.wireOp",EDGE,"E62")])],"isStart":false})]});}
            var sketch = newSketch(context, id + "F87", { "sketchPlane" : qUnion([Q0])});
            skLineSegment(sketch, "E136", {"start": v(-101.8, 177.8) * mm, "end": v(393.5, 1456.6) * mm});
            skLineSegment(sketch, "E137", {"start": v(393.5, 1456.6) * mm, "end": v(393.5, 1562.1) * mm});
            skLineSegment(sketch, "E138", {"start": v(393.5, 1562.1) * mm, "end": v(-101.8, 283.3) * mm});
            skLineSegment(sketch, "E139", {"start": v(-101.8, 283.3) * mm, "end": v(-115.1, 248.96) * mm});
            skLineSegment(sketch, "E140", {"start": v(-101.8, 177.8) * mm, "end": v(-101.8, 283.3) * mm, "construction": true});
            skLineSegment(sketch, "E141", {"start": v(393.5, 1456.6) * mm, "end": v(393.5, 177.8) * mm, "construction": true});
            skLineSegment(sketch, "E142", {"start": v(61.79, 600.17) * mm, "end": v(26.26, 613.93) * mm, "construction": true});
            skSolve(sketch);
        }
        {
            var Q0;
            Q0 = qSketchRegion(id + "F87", true);
            var Q1;
            {var subQ1=sQuery(id+"F87.wireOp",EDGE,"E136");Q1=makeQuery(id+"F87.imprint","IMPRINT",FACE,{"disambiguationData":[TD([[makeQuery(id+"F87.imprint","IMPRINT",EDGE,{"derivedFrom":subQ1}),1.0]])]});}
            var Q2;
            {var subQ0=sQuery(id+"F59.wireOp",EDGE,"E42.0");var subQ1=makeQuery(id+"F55.opPattern","COPY",FACE,{"derivedFrom":makeQuery(id+"F49.opExtrude","CAP_FACE",FACE,{"disambiguationData":[OSD([sQuery(id+"F48.wireOp",EDGE,"E28.bottom"),sQuery(id+"F48.wireOp",EDGE,"E28.top"),sQuery(id+"F48.wireOp",EDGE,"E31"),sQuery(id+"F48.wireOp",EDGE,"E32"),sQuery(id+"F48.wireOp",EDGE,"E33"),sQuery(id+"F48.wireOp",EDGE,"E34"),sQuery(id+"F48.wireOp",EDGE,"E35"),sQuery(id+"F48.wireOp",EDGE,"E36")])],"isStart":true}),"instanceName":"1"});Q2=makeQuery(id+"F62.boolean.opBoolean","MERGE",FACE,{"derivedFrom":[makeQuery(id+"F60.boolean.opBoolean","MERGE",FACE,{"derivedFrom":[subQ1,makeQuery(id+"F56.opPattern","COPY",FACE,{"derivedFrom":subQ1,"instanceName":"1"}),makeQuery(id+"F60.opExtrude","CAP_FACE",FACE,{"disambiguationData":[OSD([sQuery(id+"F59.wireOp",EDGE,"E40.bottom"),sQuery(id+"F59.wireOp",EDGE,"E40.left"),sQuery(id+"F59.wireOp",EDGE,"E40.right"),subQ0])],"isStart":true}),makeQuery(id+"F60.opExtrude","CAP_FACE",FACE,{"disambiguationData":[OSD([sQuery(id+"F59.wireOp",EDGE,"E41.bottom"),sQuery(id+"F59.wireOp",EDGE,"E41.left"),sQuery(id+"F59.wireOp",EDGE,"E41.right"),subQ0])],"isStart":true})]}),makeQuery(id+"F62.opExtrude","CAP_FACE",FACE,{"disambiguationData":[OSD([sQuery(id+"F61.wireOp",EDGE,"E44"),sQuery(id+"F61.wireOp",EDGE,"E45"),sQuery(id+"F61.wireOp",EDGE,"E46"),sQuery(id+"F61.wireOp",EDGE,"E47"),sQuery(id+"F61.wireOp",EDGE,"E48"),sQuery(id+"F61.wireOp",EDGE,"E49"),sQuery(id+"F61.wireOp",EDGE,"E50"),sQuery(id+"F61.wireOp",EDGE,"E51")])],"isStart":true}),makeQuery(id+"F62.opExtrude","CAP_FACE",FACE,{"disambiguationData":[OSD([sQuery(id+"F61.wireOp",EDGE,"E54"),sQuery(id+"F61.wireOp",EDGE,"E55"),sQuery(id+"F61.wireOp",EDGE,"E56"),sQuery(id+"F61.wireOp",EDGE,"E58"),sQuery(id+"F61.wireOp",EDGE,"E59"),sQuery(id+"F61.wireOp",EDGE,"E60"),sQuery(id+"F61.wireOp",EDGE,"E61"),sQuery(id+"F61.wireOp",EDGE,"E62")])],"isStart":true})]});}
            extrude(context, id + "F88", {"entities" : qUnion([Q0, Q1]), "endBound" : BoundingType.UP_TO_SURFACE, "oppositeDirection" : true, "endBoundEntityFace" : qUnion([Q2]), "depth" : 25.4 * mm});
        }
        {
            var Q0;
            {var subQ0=sQuery(id+"F59.wireOp",EDGE,"E42.0");var subQ1=makeQuery(id+"F55.opPattern","COPY",FACE,{"derivedFrom":makeQuery(id+"F49.opExtrude","CAP_FACE",FACE,{"disambiguationData":[OSD([sQuery(id+"F48.wireOp",EDGE,"E28.bottom"),sQuery(id+"F48.wireOp",EDGE,"E28.top"),sQuery(id+"F48.wireOp",EDGE,"E31"),sQuery(id+"F48.wireOp",EDGE,"E32"),sQuery(id+"F48.wireOp",EDGE,"E33"),sQuery(id+"F48.wireOp",EDGE,"E34"),sQuery(id+"F48.wireOp",EDGE,"E35"),sQuery(id+"F48.wireOp",EDGE,"E36")])],"isStart":false}),"instanceName":"1"});Q0=makeQuery(id+"F62.boolean.opBoolean","MERGE",FACE,{"derivedFrom":[makeQuery(id+"F60.boolean.opBoolean","MERGE",FACE,{"derivedFrom":[subQ1,makeQuery(id+"F56.opPattern","COPY",FACE,{"derivedFrom":subQ1,"instanceName":"1"}),makeQuery(id+"F60.opExtrude","CAP_FACE",FACE,{"disambiguationData":[OSD([sQuery(id+"F59.wireOp",EDGE,"E40.bottom"),sQuery(id+"F59.wireOp",EDGE,"E40.left"),sQuery(id+"F59.wireOp",EDGE,"E40.right"),subQ0])],"isStart":false}),makeQuery(id+"F60.opExtrude","CAP_FACE",FACE,{"disambiguationData":[OSD([sQuery(id+"F59.wireOp",EDGE,"E41.bottom"),sQuery(id+"F59.wireOp",EDGE,"E41.left"),sQuery(id+"F59.wireOp",EDGE,"E41.right"),subQ0])],"isStart":false})]}),makeQuery(id+"F62.opExtrude","CAP_FACE",FACE,{"disambiguationData":[OSD([sQuery(id+"F61.wireOp",EDGE,"E44"),sQuery(id+"F61.wireOp",EDGE,"E45"),sQuery(id+"F61.wireOp",EDGE,"E46"),sQuery(id+"F61.wireOp",EDGE,"E47"),sQuery(id+"F61.wireOp",EDGE,"E48"),sQuery(id+"F61.wireOp",EDGE,"E49"),sQuery(id+"F61.wireOp",EDGE,"E50"),sQuery(id+"F61.wireOp",EDGE,"E51")])],"isStart":false}),makeQuery(id+"F62.opExtrude","CAP_FACE",FACE,{"disambiguationData":[OSD([sQuery(id+"F61.wireOp",EDGE,"E54"),sQuery(id+"F61.wireOp",EDGE,"E55"),sQuery(id+"F61.wireOp",EDGE,"E56"),sQuery(id+"F61.wireOp",EDGE,"E58"),sQuery(id+"F61.wireOp",EDGE,"E59"),sQuery(id+"F61.wireOp",EDGE,"E60"),sQuery(id+"F61.wireOp",EDGE,"E61"),sQuery(id+"F61.wireOp",EDGE,"E62")])],"isStart":false})]});}
            var sketch = newSketch(context, id + "F89", { "sketchPlane" : qUnion([Q0])});
            skLineSegment(sketch, "E143.bottom", {"start": v(393.5, -419.1) * mm, "end": v(495.1, -419.1) * mm});
            skLineSegment(sketch, "E143.top", {"start": v(393.5, 2019.3) * mm, "end": v(495.1, 2019.3) * mm});
            skLineSegment(sketch, "E143.left", {"start": v(393.5, -419.1) * mm, "end": v(393.5, 2019.3) * mm});
            skLineSegment(sketch, "E143.right", {"start": v(495.1, -419.1) * mm, "end": v(495.1, 2019.3) * mm});
            skLineSegment(sketch, "E144.0", {"start": v(393.5, 1562.1) * mm, "end": v(-101.8, 283.3) * mm});
            skLineSegment(sketch, "E145.bottom", {"start": v(393.5, 1562.1) * mm, "end": v(355.4, 1562.1) * mm});
            skLineSegment(sketch, "E145.top", {"start": v(393.5, 1651) * mm, "end": v(355.4, 1651) * mm});
            skLineSegment(sketch, "E145.left", {"start": v(393.5, 1562.1) * mm, "end": v(393.5, 1651) * mm});
            skLineSegment(sketch, "E145.right", {"start": v(355.4, 1562.1) * mm, "end": v(355.4, 1651) * mm});
            skSolve(sketch);
        }
        {
            var Q0;
            {var subQ15=sQuery(id+"F89.wireOp",EDGE,"E143.bottom");Q0=makeQuery(id+"F89.imprint","IMPRINT",FACE,{"disambiguationData":[TD([[makeQuery(id+"F89.imprint","IMPRINT",EDGE,{"derivedFrom":subQ15}),1.0]])]});}
            var Q1;
            Q1=makeQuery(id+"F88.opExtrude","CAP_FACE",FACE,{"disambiguationData":[OSD([sQuery(id+"F61.wireOp",EDGE,"E56"),sQuery(id+"F87.wireOp",EDGE,"E136"),sQuery(id+"F87.wireOp",EDGE,"E137"),sQuery(id+"F87.wireOp",EDGE,"E138")])],"isStart":false});
            extrude(context, id + "F90", {"entities" : qUnion([Q0]), "endBound" : BoundingType.UP_TO_SURFACE, "oppositeDirection" : true, "endBoundEntityFace" : qUnion([Q1]), "depth" : 25.4 * mm});
        }
        {
            var Q0;
            Q0=makeQuery(id+"F89.imprint","IMPRINT",FACE,{"disambiguationData":[TD([[makeQuery(id+"F89.imprint","IMPRINT",EDGE,{"derivedFrom":sQuery(id+"F89.wireOp",EDGE,"E145.bottom")}),-1.0]])]});
            var Q1;
            Q1=makeQuery(id+"F90.opExtrude","CAP_FACE",FACE,{"disambiguationData":[OSD([sQuery(id+"F89.wireOp",EDGE,"E143.bottom"),sQuery(id+"F89.wireOp",EDGE,"E143.top"),sQuery(id+"F89.wireOp",EDGE,"E143.left"),sQuery(id+"F89.wireOp",EDGE,"E143.right"),sQuery(id+"F89.wireOp",EDGE,"E145.left")])],"isStart":false});
            extrude(context, id + "F91", {"entities" : qUnion([Q0]), "endBound" : BoundingType.UP_TO_SURFACE, "oppositeDirection" : true, "endBoundEntityFace" : qUnion([Q1]), "depth" : 25.4 * mm});
        }
    });
